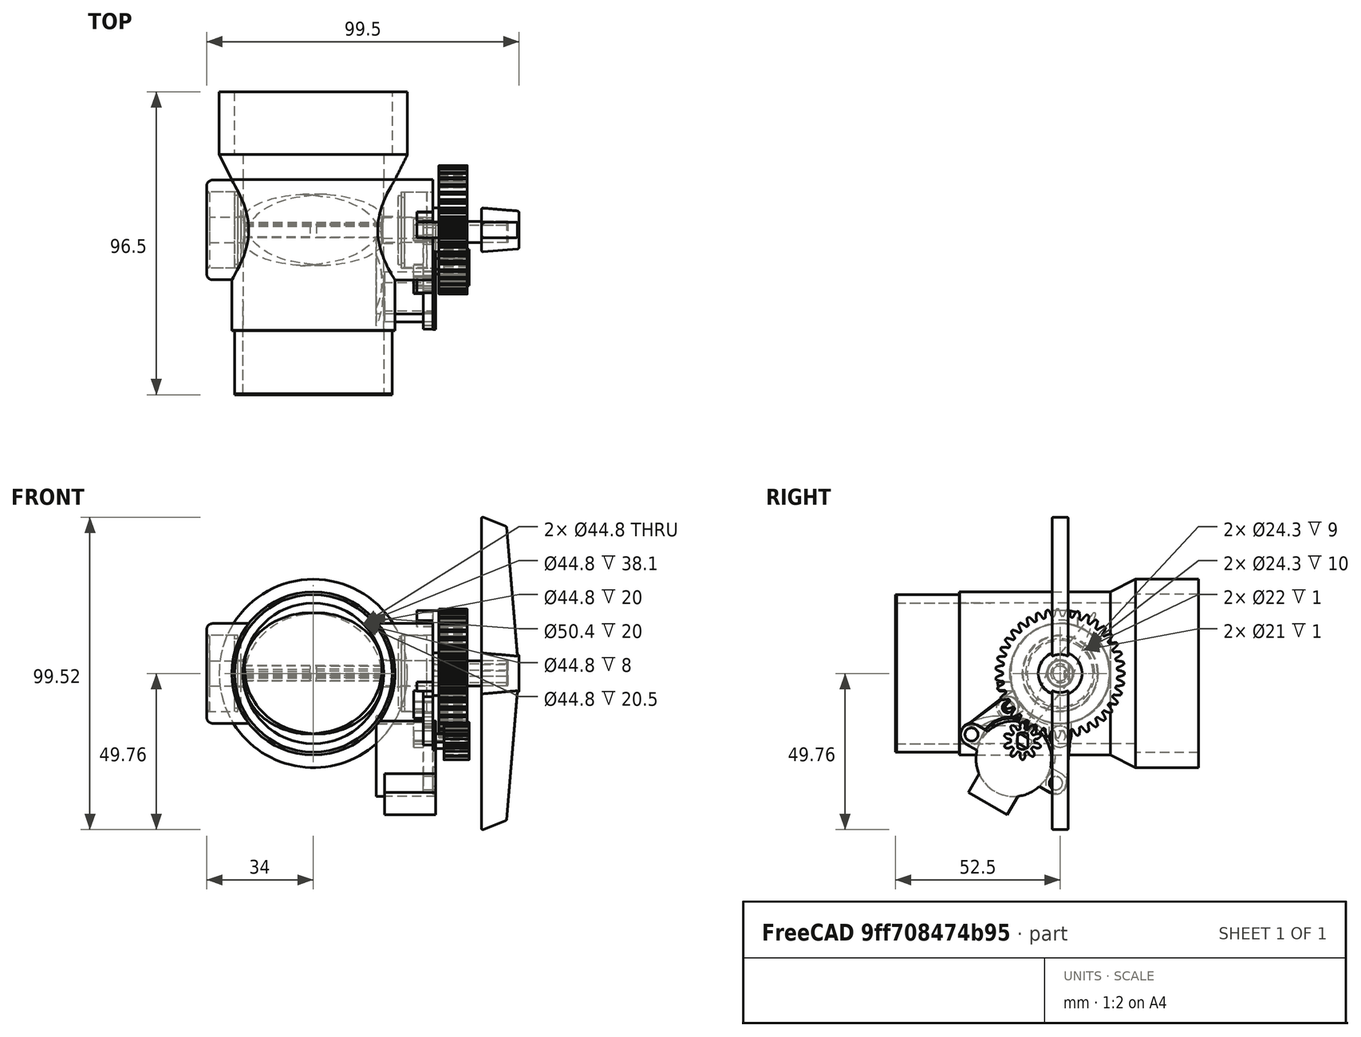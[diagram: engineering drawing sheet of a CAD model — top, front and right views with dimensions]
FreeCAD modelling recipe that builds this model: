
FCSTD DOCUMENT  (FreeCAD 0.20R29603 (Git))
Label: Pellet Sorter butterfly valve
License: All rights reserved
LicenseURL: http://en.wikipedia.org/wiki/All_rights_reserved
objects: Sketcher::SketchObject×59, PartDesign::Pad×34, PartDesign::Pocket×22, PartDesign::Body×17, PartDesign::Fillet×5, Part::Part2DObjectPython×4, PartDesign::Revolution×2, PartDesign::AdditiveLoft×2, PartDesign::Groove×1, PartDesign::Chamfer×1
note: 214 computed .brp shape members not serialized (recipe doc carries the construction recipe); baked Part::Feature solids carry a one-line shape summary decoded from their .brp

FEATURE [Sketcher::SketchObject] Sketch
  FullyConstrained = true
  MapMode = 5
  Placement = pos=(0,0,0) rot=(0.57735,0.57735,0.57735;2.0944rad)
  Support = -> [YZ_Plane]
  sketch-geometry (19):
    g0: ArcOfCircle CenterX=0 CenterY=0 CenterZ=0 NormalX=0 NormalY=0 NormalZ=1 AngleXU=0 Radius=4 StartAngle=2.97959 EndAngle=3.30359
    g1: ArcOfCircle CenterX=0 CenterY=0 CenterZ=0 NormalX=0 NormalY=0 NormalZ=1 AngleXU=0 Radius=2.5 StartAngle=0.573513 EndAngle=5.70967
    g2: LineSegment StartX=2.5 StartY=-6e-16 StartZ=0 EndX=4 EndY=-6e-16 EndZ=0
    g3: LineSegment StartX=-3.94763 StartY=0.645161 StartZ=0 EndX=-0.493454 EndY=21.7806 EndZ=0
    g4: LineSegment StartX=0.493454 StartY=21.7806 StartZ=0 EndX=3.94763 EndY=0.645161 EndZ=0
    g5: LineSegment StartX=-3.94763 StartY=-0.645161 StartZ=0 EndX=-0.493454 EndY=-21.7806 EndZ=0
    g6: LineSegment StartX=3.94763 StartY=-0.645161 StartZ=0 EndX=0.493454 EndY=-21.7806 EndZ=0
    g7: ArcOfCircle CenterX=0 CenterY=0 CenterZ=0 NormalX=0 NormalY=0 NormalZ=1 AngleXU=0 Radius=4 StartAngle=6.12119 EndAngle=6.44518
    g8: LineSegment StartX=2.1 StartY=1.35647 StartZ=0 EndX=2.1 EndY=0.45 EndZ=0
    g9: LineSegment StartX=2.1 StartY=0.45 StartZ=0 EndX=1.6 EndY=0.45 EndZ=0
    g10: LineSegment StartX=1.6 StartY=0.45 StartZ=0 EndX=1.6 EndY=-0.45 EndZ=0
    g11: LineSegment StartX=1.6 StartY=-0.45 StartZ=0 EndX=2.1 EndY=-0.45 EndZ=0
    g12: ArcOfCircle CenterX=0 CenterY=0 CenterZ=0 NormalX=0 NormalY=0 NormalZ=1 AngleXU=0 Radius=2.5 StartAngle=0 EndAngle=0.573513
    g13: ArcOfCircle CenterX=0 CenterY=0 CenterZ=0 NormalX=0 NormalY=0 NormalZ=1 AngleXU=0 Radius=2.5 StartAngle=5.70967 EndAngle=6.28319
    g14: LineSegment StartX=2.1 StartY=-0.45 StartZ=0 EndX=2.1 EndY=-1.35647 EndZ=0
    g15: ArcOfCircle CenterX=0 CenterY=21.7 CenterZ=0 NormalX=0 NormalY=0 NormalZ=1 AngleXU=0 Radius=0.5 StartAngle=0.161998 EndAngle=2.97959
    g16: ArcOfCircle CenterX=0 CenterY=-21.7 CenterZ=0 NormalX=0 NormalY=0 NormalZ=1 AngleXU=0 Radius=0.5 StartAngle=3.30359 EndAngle=6.12119
    g17: LineSegment StartX=0 StartY=21.7 StartZ=0 EndX=0 EndY=22.2 EndZ=0
    g18: LineSegment StartX=0 StartY=-21.7 StartZ=0 EndX=0 EndY=-22.2 EndZ=0
  constraints (51):
    c: Coincident(g0,g-1)
    c: Coincident(g1,g0)
    c: PointOnObject(g2,g0)
    c: Horizontal(g2)
    c: PointOnObject(g2,g-1)
    c: Distance(g2) = 1.5
    c: Diameter(g1) = 5
    c: Equal(g3,g5)
    c: Tangent(g0,g3) = 1.5708
    c: Equal(g0,g7)
    c: Tangent(g0,g5) = -1.5708
    c: Tangent(g7,g6) = 1.5708
    c: Coincident(g0,g7)
    c: Tangent(g7,g4) = 1.5708
    c: Vertical(g8)
    c: Horizontal(g9)
    c: Coincident(g10,g9)
    c: Vertical(g10)
    c: Coincident(g11,g10)
    c: Horizontal(g11)
    c: Coincident(g8,g9)
    c: Coincident(g1,g8)
    c: Coincident(g12,g0)
    c: Coincident(g12,g1)
    c: Coincident(g12,g2)
    c: Coincident(g13,g0)
    c: Coincident(g13,g1)
    c: Coincident(g13,g2)
    c: Equal(g11,g9)
    c: Coincident(g14,g11)
    c: Coincident(g14,g1)
    c: Vertical(g14)
    c: Equal(g8,g14)
    c: Distance(g0,g10) = 1.6
    c: Distance(g8,g-2) = 2.1
    c: Distance(g10) = 0.9
    c: PointOnObject(g15,g-2)
    c: PointOnObject(g16,g-2)
    c: Tangent(g15,g3) = 1.5708
    c: Tangent(g15,g4) = 1.5708
    c: Tangent(g16,g6) = 1.5708
    c: Tangent(g16,g5) = -1.5708
    c: Coincident(g17,g15)
    c: PointOnObject(g17,g15)
    c: Coincident(g18,g16)
    c: PointOnObject(g18,g16)
    c: Vertical(g18)
    c: Vertical(g17)
    c: Distance(g17,g18) = 44.4
    c: Equal(g15,g16)
    c: Diameter(g15) = 1
FEATURE [PartDesign::Pad] Pad
  Direction = (1,-2e-16,3e-16)
  Length = 44
  Length2 = 10
  Midplane = true
  Placement = pos=(0,0,0) rot=(0.57735,0.57735,0.57735;2.0944rad)
  Profile = -> Sketch
  ReferenceAxis = -> Sketch [N_Axis]
  Type = 0
FEATURE [Sketcher::SketchObject] Sketch001
  FullyConstrained = true
  MapMode = 5
  Placement = pos=(0,0,0) rot=(1,0,0;1.5708rad)
  Support = -> [XZ_Plane]
  sketch-geometry (8):
    g0: ArcOfCircle CenterX=0 CenterY=0 CenterZ=0 NormalX=0 NormalY=0 NormalZ=1 AngleXU=0 Radius=22.2 StartAngle=0.18117 EndAngle=2.96042
    g1: ArcOfCircle CenterX=0 CenterY=0 CenterZ=0 NormalX=0 NormalY=0 NormalZ=1 AngleXU=0 Radius=50 StartAngle=0 EndAngle=3.14159
    g2: LineSegment StartX=-50 StartY=6.1e-15 StartZ=0 EndX=-31.8367 EndY=0 EndZ=0
    g3: LineSegment StartX=-31.8367 StartY=0 StartZ=0 EndX=-31.8367 EndY=4 EndZ=0
    g4: LineSegment StartX=-31.8367 StartY=4 StartZ=0 EndX=-21.8367 EndY=4 EndZ=0
    g5: LineSegment StartX=21.8367 StartY=4 StartZ=0 EndX=31.8367 EndY=4 EndZ=0
    g6: LineSegment StartX=31.8367 StartY=4 StartZ=0 EndX=31.8367 EndY=0 EndZ=0
    g7: LineSegment StartX=31.8367 StartY=0 StartZ=0 EndX=50 EndY=0 EndZ=0
  constraints (24):
    c: Coincident(g0,g-1)
    c: Coincident(g1,g0)
    c: PointOnObject(g1,g-1)
    c: PointOnObject(g1,g-1)
    c: Coincident(g2,g1)
    c: PointOnObject(g2,g-1)
    c: Coincident(g3,g2)
    c: Vertical(g3)
    c: Coincident(g4,g3)
    c: Coincident(g4,g0)
    c: Horizontal(g4)
    c: Coincident(g5,g0)
    c: Horizontal(g5)
    c: Coincident(g6,g5)
    c: PointOnObject(g6,g-1)
    c: Vertical(g6)
    c: Coincident(g7,g6)
    c: Coincident(g7,g1)
    c: Diameter(g0) = 44.4
    c: Equal(g5,g4)
    c: Equal(g3,g6)
    c: Distance(g6) = 4
    c: Distance(g5) = 10
    c: Diameter(g1) = 100
FEATURE [PartDesign::Groove] Groove
  Angle = 360
  Axis = (1,0,0)
  Base = (0,0,0)
  BaseFeature = -> Pad
  Placement = pos=(0,0,0) rot=(0.57735,0.57735,0.57735;2.0944rad)
  Profile = -> Sketch001
  ReferenceAxis = -> X_Axis
  Reversed = true
FEATURE [Sketcher::SketchObject] Sketch002
  FullyConstrained = true
  MapMode = 5
  Placement = pos=(0,0,0) rot=(1,0,0;1.5708rad)
  Support = -> [XZ_Plane001]
  sketch-geometry (1):
    g0: Circle CenterX=0 CenterY=0 CenterZ=0 NormalX=0 NormalY=0 NormalZ=1 AngleXU=0 Radius=26
  constraints (2):
    c: Coincident(g0,g-1)
    c: Diameter(g0) = 52
FEATURE [PartDesign::Pad] Pad001
  Direction = (0,-1,2e-16)
  Length = 22.1
  Length2 = 16
  Placement = pos=(0,0,0) rot=(1,0,0;1.5708rad)
  Profile = -> Sketch002
  ReferenceAxis = -> Sketch002 [N_Axis]
  Type = 4
FEATURE [Sketcher::SketchObject] Sketch004
  FullyConstrained = true
  MapMode = 5
  Placement = pos=(0,0,0) rot=(1,0,0;1.5708rad)
  Support = -> [XZ_Plane001]
  sketch-geometry (4):
    g0: ArcOfCircle CenterX=0 CenterY=0 CenterZ=0 NormalX=0 NormalY=0 NormalZ=1 AngleXU=0 Radius=26 StartAngle=5.62031 EndAngle=6.28319
    g1: LineSegment StartX=20.4939 StartY=-16 StartZ=0 EndX=38 EndY=-16 EndZ=0
    g2: LineSegment StartX=38 StartY=-16 StartZ=0 EndX=38 EndY=0 EndZ=0
    g3: LineSegment StartX=38 StartY=0 StartZ=0 EndX=26 EndY=-6.4e-15 EndZ=0
  constraints (12):
    c: Coincident(g0,g-1)
    c: PointOnObject(g0,g-1)
    c: Coincident(g1,g0)
    c: Horizontal(g1)
    c: Coincident(g2,g1)
    c: PointOnObject(g2,g-1)
    c: Vertical(g2)
    c: Coincident(g3,g2)
    c: Coincident(g3,g0)
    c: Diameter(g0) = 52
    c: Distance(g3) = 12
    c: Distance(g2) = 16
FEATURE [PartDesign::Revolution] Revolution
  Angle = 360
  Axis = (1,0,0)
  Base = (0,0,0)
  BaseFeature = -> Pad001
  Placement = pos=(0,0,0) rot=(1,0,0;1.5708rad)
  Profile = -> Sketch004
  ReferenceAxis = -> Sketch004 [H_Axis]
  Reversed = true
FEATURE [Sketcher::SketchObject] Sketch006
  FullyConstrained = true
  MapMode = 5
  Placement = pos=(38,0,0) rot=(0.707107,0,0.707107;3.14159rad)
  sketch-geometry (1):
    g0: Circle CenterX=0 CenterY=0 CenterZ=0 NormalX=0 NormalY=0 NormalZ=1 AngleXU=0 Radius=12.15
  constraints (2):
    c: Coincident(g0,g-1)
    c: Diameter(g0) = 24.3
FEATURE [PartDesign::Pocket] Pocket001
  BaseFeature = -> Revolution
  Direction = (-1,0,2e-16)
  Length = 10
  Length2 = 5
  Placement = pos=(0,0,0) rot=(1,0,0;1.5708rad)
  Profile = -> Sketch006
  ReferenceAxis = -> Sketch006 [N_Axis]
  Type = 0
FEATURE [Sketcher::SketchObject] Sketch007
  FullyConstrained = true
  MapMode = 5
  Placement = pos=(28,0,0) rot=(0.707107,0,0.707107;3.14159rad)
  Support = -> [Pocket001]
  sketch-geometry (1):
    g0: Circle CenterX=0 CenterY=0 CenterZ=0 NormalX=0 NormalY=0 NormalZ=1 AngleXU=0 Radius=11
  constraints (2):
    c: Coincident(g0,g-1)
    c: Diameter(g0) = 22
FEATURE [PartDesign::Pocket] Pocket002
  BaseFeature = -> Pocket001
  Direction = (-1,0,2e-16)
  Length = 1
  Length2 = 5
  Placement = pos=(0,0,0) rot=(1,0,0;1.5708rad)
  Profile = -> Sketch007
  ReferenceAxis = -> Sketch007 [N_Axis]
  Type = 0
FEATURE [Sketcher::SketchObject] Sketch008
  FullyConstrained = true
  MapMode = 5
  Placement = pos=(27,0,-5.9e-15) rot=(0.707107,0,0.707107;3.14159rad)
  Support = -> [Pocket002]
  sketch-geometry (1):
    g0: Circle CenterX=0 CenterY=0 CenterZ=0 NormalX=0 NormalY=0 NormalZ=1 AngleXU=0 Radius=4.2
  constraints (2):
    c: Coincident(g0,g-1)
    c: Diameter(g0) = 8.4
FEATURE [PartDesign::Pocket] Pocket003
  BaseFeature = -> Pocket002
  Direction = (-1,0,2e-16)
  Length = 10
  Length2 = 5
  Placement = pos=(0,0,0) rot=(1,0,0;1.5708rad)
  Profile = -> Sketch008
  ReferenceAxis = -> Sketch008 [N_Axis]
  Type = 0
FEATURE [Sketcher::SketchObject] Sketch009
  FullyConstrained = true
  MapMode = 5
  Placement = pos=(0,0,0) rot=(0.57735,0.57735,0.57735;2.0944rad)
  Support = -> [YZ_Plane002]
  sketch-geometry (1):
    g0: Circle CenterX=0 CenterY=0 CenterZ=0 NormalX=0 NormalY=0 NormalZ=1 AngleXU=0 Radius=4
  constraints (2):
    c: Coincident(g0,g-1)
    c: Diameter(g0) = 8
FEATURE [PartDesign::Pad] Pad002
  Direction = (1,-2e-16,3e-16)
  Length = 40
  Length2 = 10
  Placement = pos=(0,0,0) rot=(0.57735,0.57735,0.57735;2.0944rad)
  Profile = -> Sketch009
  ReferenceAxis = -> Sketch009 [N_Axis]
  Type = 0
FEATURE [Sketcher::SketchObject] Sketch010
  FullyConstrained = true
  MapMode = 5
  Support = -> [XY_Plane003]
  sketch-geometry (2):
    g0: Circle CenterX=0 CenterY=0 CenterZ=0 NormalX=0 NormalY=0 NormalZ=1 AngleXU=0 Radius=4
    g1: Circle CenterX=0 CenterY=0 CenterZ=0 NormalX=0 NormalY=0 NormalZ=1 AngleXU=0 Radius=12
  constraints (4):
    c: Coincident(g0,g-1)
    c: Coincident(g1,g0)
    c: Diameter(g0) = 8
    c: Diameter(g1) = 24
FEATURE [PartDesign::Pad] Pad003
  Direction = (0,0,1)
  Length = 8.1
  Length2 = 10
  Profile = -> Sketch010
  ReferenceAxis = -> Sketch010 [N_Axis]
  Type = 0
FEATURE [PartDesign::Body] Body003  label="Body002: Bearing"
  Group = -> [Sketch010,Pad003]
  Origin = -> Origin003
  Placement = pos=(28,0,-1.4e-14) rot=(0,1,0;1.5708rad)
  Tip = -> Pad003
FEATURE [Sketcher::SketchObject] Sketch011
  FullyConstrained = true
  MapMode = 5
  Placement = pos=(0,0,0) rot=(0.57735,0.57735,0.57735;2.0944rad)
  Support = -> [YZ_Plane002]
  sketch-geometry (6):
    g0: ArcOfCircle CenterX=0 CenterY=0 CenterZ=0 NormalX=0 NormalY=0 NormalZ=1 AngleXU=0 Radius=2.3 StartAngle=0.598668 EndAngle=5.68452
    g1: LineSegment StartX=1.9 StartY=1.29615 StartZ=0 EndX=1.9 EndY=0.65 EndZ=0
    g2: LineSegment StartX=1.9 StartY=0.65 StartZ=0 EndX=1.4 EndY=0.65 EndZ=0
    g3: LineSegment StartX=1.4 StartY=0.65 StartZ=0 EndX=1.4 EndY=-0.65 EndZ=0
    g4: LineSegment StartX=1.9 StartY=-0.65 StartZ=0 EndX=1.9 EndY=-1.29615 EndZ=0
    g5: LineSegment StartX=1.4 StartY=-0.65 StartZ=0 EndX=1.9 EndY=-0.65 EndZ=0
  constraints (18):
    c: Coincident(g0,g-1)
    c: Diameter(g0) = 4.6
    c: Vertical(g1)
    c: Coincident(g2,g1)
    c: Horizontal(g2)
    c: Coincident(g3,g2)
    c: Vertical(g3)
    c: Vertical(g4)
    c: Equal(g1,g4)
    c: Coincident(g0,g4)
    c: Coincident(g0,g1)
    c: Distance(g0,g3) = 1.4
    c: Distance(g1,g-2) = 1.9
    c: Coincident(g5,g3)
    c: Coincident(g5,g4)
    c: Horizontal(g5)
    c: Equal(g2,g5)
    c: Distance(g1,g4) = 1.3
FEATURE [PartDesign::Pad] Pad004
  BaseFeature = -> Pad002
  Direction = (1,-2e-16,3e-16)
  Length = 21
  Length2 = 10
  Placement = pos=(0,0,0) rot=(0.57735,0.57735,0.57735;2.0944rad)
  Profile = -> Sketch011
  ReferenceAxis = -> Sketch011 [N_Axis]
  Reversed = true
  Type = 0
FEATURE [Sketcher::SketchObject] Sketch012
  FullyConstrained = true
  MapMode = 5
  Placement = pos=(0,0,0) rot=(1,0,0;1.5708rad)
  Support = -> [XZ_Plane001]
  sketch-geometry (4):
    g0: ArcOfCircle CenterX=0 CenterY=0 CenterZ=0 NormalX=0 NormalY=0 NormalZ=1 AngleXU=0 Radius=26 StartAngle=2.48844 EndAngle=3.14159
    g1: LineSegment StartX=-26 StartY=0 StartZ=0 EndX=-34 EndY=0 EndZ=0
    g2: LineSegment StartX=-34 StartY=0 StartZ=0 EndX=-34 EndY=15.8 EndZ=0
    g3: LineSegment StartX=-34 StartY=15.8 StartZ=0 EndX=-20.6485 EndY=15.8 EndZ=0
  constraints (12):
    c: Coincident(g0,g-1)
    c: PointOnObject(g0,g-1)
    c: Coincident(g1,g0)
    c: Horizontal(g1)
    c: Coincident(g2,g1)
    c: Vertical(g2)
    c: Coincident(g3,g2)
    c: Coincident(g3,g0)
    c: Horizontal(g3)
    c: Diameter(g0) = 52
    c: Distance(g2) = 15.8
    c: Distance(g1) = 8
FEATURE [PartDesign::Revolution] Revolution001
  Angle = 360
  Axis = (1,0,0)
  Base = (0,0,0)
  BaseFeature = -> Pocket003
  Placement = pos=(0,0,0) rot=(1,0,0;1.5708rad)
  Profile = -> Sketch012
  ReferenceAxis = -> Sketch012 [H_Axis]
FEATURE [Sketcher::SketchObject] Sketch013
  FullyConstrained = true
  MapMode = 5
  Placement = pos=(0,0,0) rot=(1,0,0;1.5708rad)
  Support = -> [XZ_Plane001]
  sketch-geometry (1):
    g0: Circle CenterX=0 CenterY=0 CenterZ=0 NormalX=0 NormalY=0 NormalZ=1 AngleXU=0 Radius=22.4
  constraints (2):
    c: Coincident(g0,g-1)
    c: Diameter(g0) = 44.8
FEATURE [PartDesign::Pocket] Pocket
  BaseFeature = -> Revolution001
  Direction = (0,1,-2e-16)
  Length = 5
  Length2 = 5
  Midplane = true
  Placement = pos=(0,0,0) rot=(1,0,0;1.5708rad)
  Profile = -> Sketch013
  ReferenceAxis = -> Sketch013 [N_Axis]
  Type = 1
FEATURE [Sketcher::SketchObject] Sketch014
  FullyConstrained = true
  MapMode = 5
  Placement = pos=(-34,0,0) rot=(0.707107,0,-0.707107;3.14159rad)
  Support = -> [Pocket]
  sketch-geometry (1):
    g0: Circle CenterX=0 CenterY=0 CenterZ=0 NormalX=0 NormalY=0 NormalZ=1 AngleXU=0 Radius=12.15
  constraints (2):
    c: Coincident(g0,g-1)
    c: Diameter(g0) = 24.3
FEATURE [PartDesign::Pocket] Pocket004
  BaseFeature = -> Pocket
  Direction = (1,0,2e-16)
  Length = 9
  Length2 = 5
  Placement = pos=(0,0,0) rot=(1,0,0;1.5708rad)
  Profile = -> Sketch014
  ReferenceAxis = -> Sketch014 [N_Axis]
  Type = 0
FEATURE [Sketcher::SketchObject] Sketch015
  FullyConstrained = true
  MapMode = 5
  Placement = pos=(-25,0,0) rot=(0.707107,0,-0.707107;3.14159rad)
  Support = -> [Pocket004]
  sketch-geometry (1):
    g0: Circle CenterX=0 CenterY=0 CenterZ=0 NormalX=0 NormalY=0 NormalZ=1 AngleXU=0 Radius=11
  constraints (2):
    c: Coincident(g0,g-1)
    c: Diameter(g0) = 22
FEATURE [PartDesign::Pocket] Pocket005
  BaseFeature = -> Pocket004
  Direction = (1,0,2e-16)
  Length = 1
  Length2 = 5
  Placement = pos=(0,0,0) rot=(1,0,0;1.5708rad)
  Profile = -> Sketch015
  ReferenceAxis = -> Sketch015 [N_Axis]
  Type = 0
FEATURE [Sketcher::SketchObject] Sketch016
  FullyConstrained = true
  MapMode = 5
  Placement = pos=(-24,0,-5.3e-15) rot=(0.707107,0,-0.707107;3.14159rad)
  Support = -> [Pocket005]
  sketch-geometry (1):
    g0: Circle CenterX=0 CenterY=0 CenterZ=0 NormalX=0 NormalY=0 NormalZ=1 AngleXU=0 Radius=4.2
  constraints (2):
    c: Coincident(g0,g-1)
    c: Diameter(g0) = 8.4
FEATURE [PartDesign::Pocket] Pocket006
  BaseFeature = -> Pocket005
  Direction = (1,0,2e-16)
  Length = 10
  Length2 = 5
  Placement = pos=(0,0,0) rot=(1,0,0;1.5708rad)
  Profile = -> Sketch016
  ReferenceAxis = -> Sketch016 [N_Axis]
  Type = 0
FEATURE [Sketcher::SketchObject] Sketch017
  FullyConstrained = true
  MapMode = 5
  Placement = pos=(0,0,0) rot=(0.57735,0.57735,0.57735;2.0944rad)
  Support = -> [YZ_Plane004]
  sketch-geometry (1):
    g0: Circle CenterX=0 CenterY=0 CenterZ=0 NormalX=0 NormalY=0 NormalZ=1 AngleXU=0 Radius=4
  constraints (2):
    c: Coincident(g0,g-1)
    c: Diameter(g0) = 8
FEATURE [PartDesign::Pad] Pad005
  Direction = (1,-2e-16,3e-16)
  Length = 12
  Length2 = 10
  Placement = pos=(0,0,0) rot=(0.57735,0.57735,0.57735;2.0944rad)
  Profile = -> Sketch017
  ReferenceAxis = -> Sketch017 [N_Axis]
  Type = 0
FEATURE [Sketcher::SketchObject] Sketch018
  FullyConstrained = true
  MapMode = 5
  Placement = pos=(0,0,0) rot=(0.57735,0.57735,0.57735;2.0944rad)
  Support = -> [YZ_Plane004]
  sketch-geometry (6):
    g0: ArcOfCircle CenterX=0 CenterY=0 CenterZ=0 NormalX=0 NormalY=0 NormalZ=1 AngleXU=0 Radius=2.3 StartAngle=0.598668 EndAngle=5.68452
    g1: LineSegment StartX=1.9 StartY=1.29615 StartZ=0 EndX=1.9 EndY=0.65 EndZ=0
    g2: LineSegment StartX=1.9 StartY=0.65 StartZ=0 EndX=1.4 EndY=0.65 EndZ=0
    g3: LineSegment StartX=1.4 StartY=0.65 StartZ=0 EndX=1.4 EndY=-0.65 EndZ=0
    g4: LineSegment StartX=1.9 StartY=-0.65 StartZ=0 EndX=1.9 EndY=-1.29615 EndZ=0
    g5: LineSegment StartX=1.4 StartY=-0.65 StartZ=0 EndX=1.9 EndY=-0.65 EndZ=0
  constraints (18):
    c: Coincident(g0,g-1)
    c: Diameter(g0) = 4.6
    c: Vertical(g1)
    c: Coincident(g2,g1)
    c: Horizontal(g2)
    c: Coincident(g3,g2)
    c: Vertical(g3)
    c: Vertical(g4)
    c: Equal(g1,g4)
    c: Coincident(g0,g4)
    c: Coincident(g0,g1)
    c: Distance(g0,g3) = 1.4
    c: Distance(g1,g-2) = 1.9
    c: Coincident(g5,g3)
    c: Coincident(g5,g4)
    c: Horizontal(g5)
    c: Equal(g2,g5)
    c: Distance(g1,g4) = 1.3
FEATURE [PartDesign::Pad] Pad006
  BaseFeature = -> Pad005
  Direction = (1,-2e-16,3e-16)
  Length = 21
  Length2 = 10
  Placement = pos=(0,0,0) rot=(0.57735,0.57735,0.57735;2.0944rad)
  Profile = -> Sketch018
  ReferenceAxis = -> Sketch018 [N_Axis]
  Reversed = true
  Type = 0
FEATURE [Sketcher::SketchObject] Sketch020
  FullyConstrained = true
  MapMode = 5
  Placement = pos=(12,-2.6e-15,2.6e-15) rot=(0.57735,0.57735,0.57735;2.0944rad)
  Support = -> [Pad006]
  sketch-geometry (1):
    g0: Circle CenterX=0 CenterY=0 CenterZ=0 NormalX=0 NormalY=0 NormalZ=1 AngleXU=0 Radius=11.9
  constraints (2):
    c: Coincident(g0,g-1)
    c: Diameter(g0) = 23.8
FEATURE [PartDesign::Pad] Pad007
  BaseFeature = -> Pad006
  Direction = (1,-9e-16,6e-16)
  Length = 1
  Length2 = 10
  Placement = pos=(0,0,0) rot=(0.57735,0.57735,0.57735;2.0944rad)
  Profile = -> Sketch020
  ReferenceAxis = -> Sketch020 [N_Axis]
  Reversed = true
  Type = 0
FEATURE [PartDesign::Body] Body004  label="Body002: Pin v0"
  Group = -> [Sketch017,Pad005,Sketch018,Pad006,Sketch020,Pad007]
  Origin = -> Origin004
  Placement = pos=(-22,0,-1.2e-14) rot=(0,1,0;3.14159rad)
  Tip = -> Pad007
FEATURE [Sketcher::SketchObject] Sketch021
  FullyConstrained = true
  MapMode = 5
  Placement = pos=(40,-8.8e-15,8.8e-15) rot=(0.57735,0.57735,0.57735;2.0944rad)
  Support = -> [Pad004]
  sketch-geometry (7):
    g0: Circle CenterX=0 CenterY=0 CenterZ=0 NormalX=0 NormalY=0 NormalZ=1 AngleXU=0 Radius=4
    g1: LineSegment StartX=1.4 StartY=-1 StartZ=0 EndX=1.4 EndY=1 EndZ=0
    g2: LineSegment StartX=1.4 StartY=1 StartZ=0 EndX=2.7 EndY=1 EndZ=0
    g3: LineSegment StartX=2.7 StartY=1 StartZ=0 EndX=2.7 EndY=2.95127 EndZ=0
    g4: LineSegment StartX=1.4 StartY=-1 StartZ=0 EndX=2.7 EndY=-1 EndZ=0
    g5: LineSegment StartX=2.7 StartY=-1 StartZ=0 EndX=2.7 EndY=-2.95127 EndZ=0
    g6: ArcOfCircle CenterX=0 CenterY=0 CenterZ=0 NormalX=0 NormalY=0 NormalZ=1 AngleXU=0 Radius=4 StartAngle=5.45335 EndAngle=7.11302
  constraints (20):
    c: Coincident(g0,g-1)
    c: Vertical(g1)
    c: Coincident(g2,g1)
    c: Horizontal(g2)
    c: Coincident(g3,g2)
    c: PointOnObject(g3,g0)
    c: Vertical(g3)
    c: Coincident(g4,g1)
    c: Horizontal(g4)
    c: Coincident(g5,g4)
    c: Vertical(g5)
    c: Equal(g3,g5)
    c: Equal(g4,g2)
    c: Distance(g0,g1) = 1.4
    c: Distance(g2,g4) = 2
    c: Distance(g4,g-2) = 2.7
    c: Diameter(g0) = 8
    c: Coincident(g6,g0)
    c: Coincident(g6,g3)
    c: Coincident(g6,g5)
FEATURE [PartDesign::Pocket] Pocket007
  BaseFeature = -> Pad004
  Direction = (-1,9e-16,-6e-16)
  Length = 24
  Length2 = 5
  Placement = pos=(0,0,0) rot=(0.57735,0.57735,0.57735;2.0944rad)
  Profile = -> Sketch021
  ReferenceAxis = -> Sketch021 [N_Axis]
  Type = 0
FEATURE [PartDesign::Body] Body002  label="Body002: Shaft v0"
  Group = -> [Sketch009,Pad002,Sketch011,Pad004,Sketch021,Pocket007]
  Origin = -> Origin002
  Placement = pos=(22,0,0) rot=(0,0,1;0rad)
  Tip = -> Pocket007
FEATURE [PartDesign::Chamfer] Chamfer
  Angle = 45
  Base = -> Groove [Edge27,Edge26,Edge29,Edge11,Edge28,Edge46,Edge44,Edge21,Edge47,Edge45]
  BaseFeature = -> Groove
  ChamferType = 1
  FlipDirection = true
  Placement = pos=(0,0,0) rot=(0.57735,0.57735,0.57735;2.0944rad)
  Size = 0.16
  Size2 = 1
  SupportTransform = false
  UseAllEdges = false
FEATURE [PartDesign::Body] Body  label="Body: Butterfly v0"
  Group = -> [Sketch,Pad,Sketch001,Groove,Chamfer]
  Origin = -> Origin
  Placement = pos=(0,0,0) rot=(-1,0,0;0.523599rad)
  Tip = -> Chamfer
FEATURE [Sketcher::SketchObject] Sketch060
  AttachmentOffset = pos=(0,0,0) rot=(0,0,-1;3.14159rad)
  FullyConstrained = true
  MapMode = 5
  Placement = pos=(38,0,0) rot=(0,1,0;1.5708rad)
  Support = -> [Pocket006]
  sketch-geometry (8):
    g0: ArcOfCircle CenterX=0 CenterY=0 CenterZ=0 NormalX=0 NormalY=0 NormalZ=1 AngleXU=0 Radius=16 StartAngle=4.88195 EndAngle=5.07664
    g1: LineSegment StartX=2.7 StartY=-15.7705 StartZ=0 EndX=2.7 EndY=-19.9683 EndZ=0
    g2: LineSegment StartX=5.7 StartY=-14.9503 StartZ=0 EndX=5.7 EndY=-19.327 EndZ=0
    g3: ArcOfCircle CenterX=0 CenterY=0 CenterZ=0 NormalX=0 NormalY=0 NormalZ=1 AngleXU=0 Radius=20.15 StartAngle=4.84679 EndAngle=4.99918
    g4: ArcOfCircle CenterX=0 CenterY=0 CenterZ=0 NormalX=0 NormalY=0 NormalZ=1 AngleXU=0 Radius=16 StartAngle=2.77734 EndAngle=2.97203
    g5: ArcOfCircle CenterX=0 CenterY=0 CenterZ=0 NormalX=0 NormalY=0 NormalZ=1 AngleXU=0 Radius=20.15 StartAngle=2.8548 EndAngle=3.00719
    g6: LineSegment StartX=-19.9683 StartY=2.7 StartZ=0 EndX=-15.7705 EndY=2.7 EndZ=0
    g7: LineSegment StartX=-14.9503 StartY=5.7 StartZ=0 EndX=-19.327 EndY=5.7 EndZ=0
  constraints (24):
    c: Coincident(g0,g-1)
    c: Diameter(g0) = 32
    c: Coincident(g1,g0)
    c: Vertical(g1)
    c: Coincident(g2,g0)
    c: Vertical(g2)
    c: Coincident(g3,g0)
    c: Coincident(g3,g1)
    c: Coincident(g3,g2)
    c: Diameter(g3) = 40.3
    c: Distance(g0,g-2) = 2.7
    c: Distance(g2,g1) = 3
    c: Coincident(g4,g0)
    c: Coincident(g5,g0)
    c: Coincident(g6,g5)
    c: Coincident(g6,g4)
    c: Horizontal(g6)
    c: Coincident(g7,g4)
    c: Horizontal(g7)
    c: Coincident(g5,g7)
    c: Equal(g4,g0)
    c: Equal(g5,g3)
    c: Equal(g7,g2)
    c: Equal(g6,g1)
FEATURE [PartDesign::Pad] Pad008
  BaseFeature = -> Pocket006
  Direction = (1,0,-2e-16)
  Length = 5
  Length2 = 10
  Placement = pos=(0,0,0) rot=(1,0,0;1.5708rad)
  Profile = -> Sketch060
  ReferenceAxis = -> Sketch060 [N_Axis]
  Reversed = true
  Type = 0
FEATURE [Sketcher::SketchObject] Sketch031
  FullyConstrained = true
  MapMode = 5
  Support = -> [XY_Plane006]
  sketch-geometry (14):
    g0: ArcOfCircle CenterX=0 CenterY=0 CenterZ=0 NormalX=0 NormalY=0 NormalZ=1 AngleXU=0 Radius=7 StartAngle=1.936 EndAngle=7.48877
    g1: LineSegment StartX=-2.5 StartY=6.53835 StartZ=0 EndX=-2.5 EndY=20 EndZ=0
    g2: LineSegment StartX=2.5 StartY=6.53835 StartZ=0 EndX=2.5 EndY=20 EndZ=0
    g3: LineSegment StartX=2.5 StartY=20 StartZ=0 EndX=-2.5 EndY=20 EndZ=0
    g4: LineSegment StartX=0 StartY=0 StartZ=0 EndX=0 EndY=20 EndZ=0
    g5: ArcOfCircle CenterX=0 CenterY=0 CenterZ=0 NormalX=0 NormalY=0 NormalZ=1 AngleXU=0 Radius=4 StartAngle=0.795399 EndAngle=5.48779
    g6: LineSegment StartX=2.8 StartY=-2.85657 StartZ=0 EndX=2.8 EndY=-0.85 EndZ=0
    g7: LineSegment StartX=2.8 StartY=-0.85 StartZ=0 EndX=1.5 EndY=-0.85 EndZ=0
    g8: LineSegment StartX=1.5 StartY=-0.85 StartZ=0 EndX=1.5 EndY=0.85 EndZ=0
    g9: LineSegment StartX=1.5 StartY=0.85 StartZ=0 EndX=2.8 EndY=0.85 EndZ=0
    g10: LineSegment StartX=2.8 StartY=0.85 StartZ=0 EndX=2.8 EndY=2.85657 EndZ=0
    g11: LineSegment StartX=-4 StartY=0 StartZ=0 EndX=1.5 EndY=0 EndZ=0
    g12: LineSegment StartX=2.8 StartY=-0.85 StartZ=0 EndX=2.8 EndY=0.85 EndZ=0
    g13: LineSegment StartX=2.8 StartY=0 StartZ=0 EndX=-4 EndY=0 EndZ=0
  constraints (43):
    c: Vertical(g1)
    c: Vertical(g2)
    c: Coincident(g3,g2)
    c: Coincident(g3,g1)
    c: Horizontal(g3)
    c: Coincident(g0,g2)
    c: Coincident(g0,g1)
    c: Diameter(g0) = 14
    c: Distance(g3) = 5
    c: Equal(g1,g2)
    c: Coincident(g4,g0)
    c: Vertical(g4)
    c: Distance(g4) = 20
    c: PointOnObject(g4,g3)
    c: Coincident(g0,g-1)
    c: Coincident(g5,g0)
    c: Diameter(g5) = 8
    c: Vertical(g6)
    c: Coincident(g7,g6)
    c: Horizontal(g7)
    c: Vertical(g8)
    c: Coincident(g9,g8)
    c: Horizontal(g9)
    c: Coincident(g10,g9)
    c: Vertical(g10)
    c: PointOnObject(g11,g5)
    c: PointOnObject(g11,g8)
    c: Horizontal(g11)
    c: Perpendicular(g5,g11)
    c: Distance(g11) = 5.5
    c: Coincident(g12,g6)
    c: Coincident(g12,g9)
    c: Vertical(g12)
    c: PointOnObject(g13,g12)
    c: PointOnObject(g13,g5)
    c: Horizontal(g13)
    c: Perpendicular(g5,g13)
    c: Distance(g13) = 6.8
    c: Distance(g12) = 1.7
    c: Equal(g10,g6)
    c: Coincident(g7,g8)
    c: Coincident(g5,g6)
    c: Coincident(g5,g10)
FEATURE [PartDesign::Pad] Pad011
  Direction = (0,0,1)
  Length = 2
  Length2 = 10
  Profile = -> Sketch031
  ReferenceAxis = -> Sketch031 [N_Axis]
  Type = 0
FEATURE [Sketcher::SketchObject] Sketch032
  FullyConstrained = true
  MapMode = 5
  Placement = pos=(0,0,0) rot=(1,0,0;3.14159rad)
  Support = -> [Pad011]
  sketch-geometry (5):
    g0: LineSegment StartX=0 StartY=-20 StartZ=0 EndX=2.5 EndY=-20 EndZ=0
    g1: LineSegment StartX=0 StartY=-20 StartZ=0 EndX=-2.5 EndY=-20 EndZ=0
    g2: LineSegment StartX=-2.5 StartY=-20 StartZ=0 EndX=-2.5 EndY=-16.8152 EndZ=0
    g3: LineSegment StartX=2.5 StartY=-20 StartZ=0 EndX=2.5 EndY=-16.8152 EndZ=0
    g4: ArcOfCircle CenterX=0 CenterY=0 CenterZ=0 NormalX=0 NormalY=0 NormalZ=1 AngleXU=0 Radius=17 StartAngle=4.56479 EndAngle=4.85998
  constraints (15):
    c: PointOnObject(g0,g-2)
    c: Horizontal(g0)
    c: Coincident(g1,g0)
    c: Horizontal(g1)
    c: Coincident(g2,g1)
    c: Vertical(g2)
    c: Coincident(g3,g0)
    c: Vertical(g3)
    c: Coincident(g4,g-1)
    c: Coincident(g4,g3)
    c: Coincident(g4,g2)
    c: Equal(g3,g2)
    c: Distance(g0,g1) = 5
    c: Diameter(g4) = 34
    c: Distance(g4,g0) = 20
FEATURE [PartDesign::Pad] Pad012
  BaseFeature = -> Pad011
  Direction = (0,0,-1)
  Length = 5
  Length2 = 10
  Profile = -> Sketch032
  ReferenceAxis = -> Sketch032 [N_Axis]
  Type = 0
FEATURE [PartDesign::Body] Body006  label="Body006: Ball stop"
  Group = -> [Sketch031,Pad011,Sketch032,Pad012]
  Origin = -> Origin006
  Placement = pos=(38,-2.8e-14,-2.6e-14) rot=(0.57735,0.57735,0.57735;2.0944rad)
  Tip = -> Pad012
FEATURE [PartDesign::Fillet] Fillet
  Base = -> Pad008 [Edge24]
  BaseFeature = -> Pad008
  Placement = pos=(0,0,0) rot=(1,0,0;1.5708rad)
  Radius = 2
  SupportTransform = false
  UseAllEdges = false
FEATURE [Sketcher::SketchObject] Sketch061
  FullyConstrained = false
  MapMode = 5
  Placement = pos=(38,0,0) rot=(0.707107,0,0.707107;3.14159rad)
  Support = -> [Fillet]
  sketch-geometry (4):
    g0: Circle CenterX=-27.2 CenterY=14.8 CenterZ=0 NormalX=0 NormalY=0 NormalZ=1 AngleXU=0 Radius=12
    g1: LineSegment StartX=-27.2 StartY=14.8 StartZ=0 EndX=0 EndY=0 EndZ=0
    g2: LineSegment StartX=-27.2 StartY=14.8 StartZ=0 EndX=-34.6521 EndY=1.89256 EndZ=0
    g3: LineSegment StartX=-27.2 StartY=14.8 StartZ=0 EndX=-19.5784 EndY=28.001 EndZ=0
  constraints (9):
    c: Diameter(g0) = 24
    c: Distance(g0,g-2) = 27.2
    c: Distance(g0,g-1) = 14.8
    c: Coincident(g1,g0)
    c: Coincident(g1,g-1)
    c: Coincident(g2,g0)
    c: Coincident(g3,g0)
    c: Parallel(g3,g2)
    c: Angle(g-1,g2) = 1.0472
FEATURE [Sketcher::SketchObject] Sketch034
  FullyConstrained = true
  MapMode = 5
  Support = -> [XY_Plane007]
  sketch-geometry (1):
    g0: Circle CenterX=0 CenterY=0 CenterZ=0 NormalX=0 NormalY=0 NormalZ=1 AngleXU=0 Radius=12
  constraints (2):
    c: Coincident(g0,g-1)
    c: Diameter(g0) = 24
FEATURE [PartDesign::Pad] Pad014
  Direction = (0,0,1)
  Length = 19
  Length2 = 10
  Profile = -> Sketch034
  ReferenceAxis = -> Sketch034 [N_Axis]
  Type = 0
FEATURE [Sketcher::SketchObject] Sketch035
  FullyConstrained = true
  MapMode = 5
  Placement = pos=(0,0,19) rot=(0,0,1;0rad)
  Support = -> [Pad014]
  sketch-geometry (5):
    g0: LineSegment StartX=-7.15 StartY=-6.5 StartZ=0 EndX=-7.15 EndY=-16.5 EndZ=0
    g1: LineSegment StartX=-7.15 StartY=-16.5 StartZ=0 EndX=7.15 EndY=-16.5 EndZ=0
    g2: LineSegment StartX=7.15 StartY=-16.5 StartZ=0 EndX=7.15 EndY=-6.5 EndZ=0
    g3: LineSegment StartX=7.15 StartY=-6.5 StartZ=0 EndX=-7.15 EndY=-6.5 EndZ=0
    g4: GeomPoint X=0 Y=-11.5 Z=0
  constraints (13):
    c: Coincident(g0,g1)
    c: Coincident(g1,g2)
    c: Coincident(g2,g3)
    c: Coincident(g3,g0)
    c: Horizontal(g1)
    c: Horizontal(g3)
    c: Vertical(g0)
    c: Vertical(g2)
    c: Symmetric(g1,g0,g4)
    c: PointOnObject(g4,g-2)
    c: DistanceY(g1,g-1) = 16.5
    c: DistanceX(g1,g1) = 14.3
    c: Distance(g2) = 10
FEATURE [PartDesign::Pad] Pad015
  BaseFeature = -> Pad014
  Direction = (0,0,1)
  Length = 16.3
  Length2 = 10
  Profile = -> Sketch035
  ReferenceAxis = -> Sketch035 [N_Axis]
  Reversed = true
  Type = 0
FEATURE [Sketcher::SketchObject] Sketch036
  FullyConstrained = true
  MapMode = 5
  Placement = pos=(0,0,19) rot=(0,0,1;0rad)
  Support = -> [Pad015]
  sketch-geometry (6):
    g0: Circle CenterX=15.5 CenterY=0 CenterZ=0 NormalX=0 NormalY=0 NormalZ=1 AngleXU=0 Radius=2.1
    g1: Circle CenterX=-15.5 CenterY=0 CenterZ=0 NormalX=0 NormalY=0 NormalZ=1 AngleXU=0 Radius=2.1
    g2: ArcOfCircle CenterX=15.5 CenterY=0 CenterZ=0 NormalX=0 NormalY=0 NormalZ=1 AngleXU=0 Radius=3.5 StartAngle=4.71239 EndAngle=7.85398
    g3: ArcOfCircle CenterX=-15.5 CenterY=0 CenterZ=0 NormalX=0 NormalY=0 NormalZ=1 AngleXU=0 Radius=3.5 StartAngle=1.5708 EndAngle=4.71239
    g4: LineSegment StartX=15.5 StartY=3.5 StartZ=0 EndX=-15.5 EndY=3.5 EndZ=0
    g5: LineSegment StartX=-15.5 StartY=-3.5 StartZ=0 EndX=15.5 EndY=-3.5 EndZ=0
  constraints (15):
    c: PointOnObject(g0,g-1)
    c: PointOnObject(g1,g-1)
    c: Equal(g0,g1)
    c: Diameter(g0) = 4.2
    c: Distance(g0,g1) = 31
    c: Distance(g-1,g0) = 15.5
    c: Coincident(g2,g0)
    c: Diameter(g2) = 7
    c: Coincident(g3,g1)
    c: Horizontal(g4)
    c: Tangent(g2,g4) = -1.5708
    c: Tangent(g3,g5) = -1.5708
    c: Coincident(g3,g4)
    c: Tangent(g3,g4,g3) = -1.5708
    c: Tangent(g2,g5) = -1.5708
FEATURE [PartDesign::Pad] Pad016
  BaseFeature = -> Pad015
  Direction = (0,0,1)
  Length = 1
  Length2 = 10
  Profile = -> Sketch036
  ReferenceAxis = -> Sketch036 [N_Axis]
  Reversed = true
  Type = 0
FEATURE [Sketcher::SketchObject] Sketch037
  FullyConstrained = true
  MapMode = 5
  Placement = pos=(0,0,19) rot=(0,0,1;0rad)
  Support = -> [Pad016]
  sketch-geometry (4):
    g0: ArcOfCircle CenterX=0 CenterY=6.5 CenterZ=0 NormalX=0 NormalY=0 NormalZ=1 AngleXU=0 Radius=2.5 StartAngle=2.49809 EndAngle=3.78509
    g1: LineSegment StartX=-2 StartY=8 StartZ=0 EndX=2 EndY=8 EndZ=0
    g2: LineSegment StartX=-2 StartY=5 StartZ=0 EndX=2 EndY=5 EndZ=0
    g3: ArcOfCircle CenterX=0 CenterY=6.5 CenterZ=0 NormalX=0 NormalY=0 NormalZ=1 AngleXU=0 Radius=2.5 StartAngle=5.63968 EndAngle=6.92669
  constraints (13):
    c: PointOnObject(g0,g-2)
    c: Distance(g0,g-1) = 6.5
    c: Diameter(g0) = 5
    c: Horizontal(g1)
    c: Horizontal(g2)
    c: DistanceY(g2,g1) = 3
    c: DistanceY(g0,g1) = 1.5
    c: Coincident(g3,g1)
    c: Coincident(g0,g1)
    c: Equal(g0,g3)
    c: Coincident(g0,g2)
    c: Coincident(g3,g2)
    c: Coincident(g0,g3)
FEATURE [PartDesign::Pad] Pad017
  BaseFeature = -> Pad016
  Direction = (0,0,1)
  Length = 10
  Length2 = 10
  Profile = -> Sketch037
  ReferenceAxis = -> Sketch037 [N_Axis]
  Type = 0
FEATURE [Sketcher::SketchObject] Sketch043  label="Sketch043: Gear aid"
  FullyConstrained = false
  MapMode = 5
  Placement = pos=(0,0,29) rot=(0,0,1;0rad)
  Support = -> [Pad017]
  sketch-geometry (4):
    g0: LineSegment StartX=0 StartY=6.50621 StartZ=0 EndX=0 EndY=57.9462 EndZ=0
    g1: Circle CenterX=0 CenterY=57.9462 CenterZ=0 NormalX=0 NormalY=0 NormalZ=1 AngleXU=0 Radius=22.3949
    g2: Circle CenterX=0 CenterY=6.50621 CenterZ=0 NormalX=0 NormalY=0 NormalZ=1 AngleXU=0 Radius=2.48851
    g3: Circle CenterX=0 CenterY=6.50621 CenterZ=0 NormalX=0 NormalY=0 NormalZ=1 AngleXU=0 Radius=15.9809
  constraints (6):
    c: PointOnObject(g0,g-2)
    c: PointOnObject(g0,g-2)
    c: Coincident(g1,g0)
    c: Coincident(g2,g0)
    c: Distance(g0) = 51.44
    c: Coincident(g3,g0)
FEATURE [PartDesign::Body] Body007  label="Body002: Motor"
  Group = -> [Sketch034,Pad014,Sketch035,Pad015,Sketch036,Pad016,Sketch037,Pad017,Sketch043]
  Origin = -> Origin007
  Placement = pos=(20.0052,-14.8071,-27.2) rot=(0.447214,0.774597,0.447214;1.82348rad)
  Tip = -> Pad017
FEATURE [Sketcher::SketchObject] Sketch062
  AttachmentOffset = pos=(0,0,20) rot=(0,0,1;0rad)
  FullyConstrained = false
  MapMode = 5
  Placement = pos=(20,-4.4e-15,4.4e-15) rot=(0.57735,0.57735,0.57735;2.0944rad)
  Support = -> [YZ_Plane001]
  sketch-geometry (4):
    g0: Circle CenterX=-14.8 CenterY=-27.2 CenterZ=0 NormalX=0 NormalY=0 NormalZ=1 AngleXU=0 Radius=12.5
    g1: LineSegment StartX=0 StartY=0 StartZ=0 EndX=-14.8 EndY=-27.2 EndZ=0
    g2: LineSegment StartX=-14.8 StartY=-27.2 StartZ=0 EndX=-27.7105 EndY=-50.9274 EndZ=0
    g3: Circle CenterX=-16.4728 CenterY=-30.2744 CenterZ=0 NormalX=0 NormalY=0 NormalZ=1 AngleXU=0 Radius=16
  constraints (10):
    c: Distance(g0,g-2) = 14.8
    c: Distance(g0,g-1) = 27.2
    c: Diameter(g0) = 25
    c: Coincident(g1,g-1)
    c: Coincident(g1,g0)
    c: Coincident(g2,g0)
    c: Parallel(g1,g2)
    c: PointOnObject(g3,g2)
    c: Tangent(g3,g0)
    c: Diameter(g3) = 32
FEATURE [Sketcher::SketchObject] Sketch063
  AttachmentOffset = pos=(0,0,-3) rot=(0,0,1;0rad)
  FullyConstrained = true
  MapMode = 5
  Placement = pos=(35,0,1e-15) rot=(0.707107,0,0.707107;3.14159rad)
  sketch-geometry (13):
    g0: Circle CenterX=-10.8627 CenterY=16.7929 CenterZ=0 NormalX=0 NormalY=0 NormalZ=1 AngleXU=0 Radius=1.7
    g1: Circle CenterX=-20 CenterY=0 CenterZ=0 NormalX=0 NormalY=0 NormalZ=1 AngleXU=0 Radius=1.7
    g2: LineSegment StartX=-27.2 StartY=14.8 StartZ=0 EndX=0 EndY=0 EndZ=0
    g3: LineSegment StartX=-10.8627 StartY=16.7929 StartZ=0 EndX=-15.4313 EndY=8.39646 EndZ=0
    g4: LineSegment StartX=-20 StartY=0 StartZ=0 EndX=-15.4313 EndY=8.39646 EndZ=0
    g5: ArcOfCircle CenterX=-20 CenterY=0 CenterZ=0 NormalX=0 NormalY=0 NormalZ=1 AngleXU=0 Radius=3.5 StartAngle=1.5708 EndAngle=4.71239
    g6: ArcOfCircle CenterX=-10.8627 CenterY=16.7929 CenterZ=0 NormalX=0 NormalY=0 NormalZ=1 AngleXU=0 Radius=3.5 StartAngle=0.574165 EndAngle=3.71576
    g7: LineSegment StartX=-20 StartY=3.5 StartZ=0 EndX=-15.6125 EndY=3.5 EndZ=0
    g8: ArcOfCircle CenterX=0 CenterY=0 CenterZ=0 NormalX=0 NormalY=0 NormalZ=1 AngleXU=0 Radius=16 StartAngle=2.92106 EndAngle=3.36213
    g9: ArcOfCircle CenterX=0 CenterY=0 CenterZ=0 NormalX=0 NormalY=0 NormalZ=1 AngleXU=0 Radius=16 StartAngle=1.92443 EndAngle=2.36549
    g10: LineSegment StartX=-13.8014 StartY=14.892 StartZ=0 EndX=-11.4184 EndY=11.208 EndZ=0
    g11: LineSegment StartX=-7.92391 StartY=18.6939 StartZ=0 EndX=-5.54091 EndY=15.0099 EndZ=0
    g12: LineSegment StartX=-20 StartY=-3.5 StartZ=0 EndX=-15.6125 EndY=-3.5 EndZ=0
  constraints (34):
    c: Coincident(g2,g-1)
    c: Distance(g2,g-1) = 14.8
    c: Distance(g2,g-2) = 27.2
    c: Coincident(g3,g0)
    c: PointOnObject(g3,g2)
    c: Coincident(g4,g1)
    c: Coincident(g4,g3)
    c: Perpendicular(g2,g3)
    c: Perpendicular(g4,g2)
    c: Equal(g3,g4)
    c: Diameter(g0) = 3.4
    c: Equal(g0,g1)
    c: PointOnObject(g1,g-1)
    c: Distance(g1,g-2) = 20
    c: Coincident(g5,g1)
    c: Coincident(g6,g0)
    c: Horizontal(g7)
    c: Coincident(g8,g2)
    c: Coincident(g8,g7)
    c: Coincident(g9,g8)
    c: Coincident(g10,g9)
    c: Coincident(g12,g8)
    c: Horizontal(g12)
    c: Diameter(g5) = 7
    c: Equal(g5,g6)
    c: Equal(g10,g12)
    c: Equal(g7,g11)
    c: Equal(g9,g8)
    c: Tangent(g7,g5) = 1.5708
    c: Tangent(g11,g6) = 1.5708
    c: Tangent(g10,g6) = -1.5708
    c: Tangent(g12,g5) = -1.5708
    c: Coincident(g11,g9)
    c: Diameter(g8) = 32
FEATURE [PartDesign::Pad] Pad018
  BaseFeature = -> Fillet
  Direction = (1,0,-2e-16)
  Length = 3
  Length2 = 10
  Placement = pos=(0,0,0) rot=(1,0,0;1.5708rad)
  Profile = -> Sketch063
  ReferenceAxis = -> Sketch063 [N_Axis]
  Reversed = true
  Type = 0
FEATURE [Sketcher::SketchObject] Sketch064
  FullyConstrained = true
  MapMode = 5
  Placement = pos=(0,0,0) rot=(0.57735,0.57735,0.57735;2.0944rad)
  Support = -> [YZ_Plane008]
  sketch-geometry (6):
    g0: Circle CenterX=0 CenterY=0 CenterZ=0 NormalX=0 NormalY=0 NormalZ=1 AngleXU=0 Radius=1.7
    g1: ArcOfCircle CenterX=0 CenterY=0 CenterZ=0 NormalX=0 NormalY=0 NormalZ=1 AngleXU=0 Radius=3.25 StartAngle=6.19048 EndAngle=9.93442
    g2: LineSegment StartX=3.23604 StartY=-0.300876 StartZ=0 EndX=1.84604 EndY=-15.2509 EndZ=0
    g3: ArcOfCircle CenterX=-1.39 CenterY=-14.95 CenterZ=0 NormalX=0 NormalY=0 NormalZ=1 AngleXU=0 Radius=3.25 StartAngle=2.44653 EndAngle=6.19048
    g4: ArcOfCircle CenterX=-11.5662 CenterY=-6.46424 CenterZ=0 NormalX=0 NormalY=0 NormalZ=1 AngleXU=0 Radius=10 StartAngle=5.58812 EndAngle=6.79283
    g5: Circle CenterX=-1.39 CenterY=-14.95 CenterZ=0 NormalX=0 NormalY=0 NormalZ=1 AngleXU=0 Radius=2.15
  constraints (14):
    c: Diameter(g0) = 3.4
    c: Coincident(g1,g0)
    c: Diameter(g1) = 6.5
    c: Coincident(g0,g-1)
    c: Distance(g3,g-1) = 14.95
    c: Diameter(g3) = 6.5
    c: Distance(g3,g-2) = 1.39
    c: Coincident(g5,g3)
    c: Diameter(g5) = 4.3
    c: Diameter(g4) = 20
    c: Tangent(g1,g4) = 1.5708
    c: Tangent(g1,g2) = 1.5708
    c: Tangent(g3,g2) = 1.5708
    c: Tangent(g3,g4) = 1.5708
FEATURE [PartDesign::Pad] Pad019
  Direction = (1,-2e-16,3e-16)
  Length = 3
  Length2 = 10
  Placement = pos=(0,0,0) rot=(0.57735,0.57735,0.57735;2.0944rad)
  Profile = -> Sketch064
  ReferenceAxis = -> Sketch064 [N_Axis]
  Type = 0
FEATURE [PartDesign::Body] Body008  label="Body008: Motor link A v0"
  Group = -> [Sketch064,Pad019]
  Origin = -> Origin008
  Placement = pos=(35,0,-20) rot=(0,0,1;0rad)
  Tip = -> Pad019
FEATURE [Sketcher::SketchObject] Sketch065
  FullyConstrained = true
  MapMode = 5
  Placement = pos=(0,0,0) rot=(0.57735,0.57735,0.57735;2.0944rad)
  Support = -> [YZ_Plane009]
  sketch-geometry (6):
    g0: Circle CenterX=0 CenterY=0 CenterZ=0 NormalX=0 NormalY=0 NormalZ=1 AngleXU=0 Radius=1.7
    g1: ArcOfCircle CenterX=0 CenterY=0 CenterZ=0 NormalX=0 NormalY=0 NormalZ=1 AngleXU=0 Radius=3.5 StartAngle=6.14586 EndAngle=9.88376
    g2: LineSegment StartX=3.46705 StartY=-0.479131 StartZ=0 EndX=1.5094 EndY=-14.6449 EndZ=0
    g3: ArcOfCircle CenterX=-1.71 CenterY=-14.2 CenterZ=0 NormalX=0 NormalY=0 NormalZ=1 AngleXU=0 Radius=3.25 StartAngle=2.47246 EndAngle=6.14586
    g4: ArcOfCircle CenterX=-12.1028 CenterY=-5.98099 CenterZ=0 NormalX=0 NormalY=0 NormalZ=1 AngleXU=0 Radius=10 StartAngle=5.61406 EndAngle=6.74217
    g5: Circle CenterX=-1.71 CenterY=-14.2 CenterZ=0 NormalX=0 NormalY=0 NormalZ=1 AngleXU=0 Radius=2.15
  constraints (14):
    c: Diameter(g0) = 3.4
    c: Coincident(g1,g0)
    c: Diameter(g1) = 7
    c: Coincident(g0,g-1)
    c: Diameter(g3) = 6.5
    c: Coincident(g5,g3)
    c: Diameter(g5) = 4.3
    c: Diameter(g4) = 20
    c: Tangent(g1,g4) = 1.5708
    c: Tangent(g1,g2) = 1.5708
    c: Tangent(g3,g2) = 1.5708
    c: Tangent(g3,g4) = 1.5708
    c: Distance(g3,g-2) = 1.71
    c: Distance(g3,g-1) = 14.2
FEATURE [PartDesign::Pad] Pad020
  Direction = (1,-2e-16,3e-16)
  Length = 3
  Length2 = 10
  Placement = pos=(0,0,0) rot=(0.57735,0.57735,0.57735;2.0944rad)
  Profile = -> Sketch065
  ReferenceAxis = -> Sketch065 [N_Axis]
  Type = 0
FEATURE [PartDesign::Body] Body009  label="Body008: Motor link B v0"
  Group = -> [Sketch065,Pad020]
  Origin = -> Origin009
  Placement = pos=(38,-16.7835,-10.875) rot=(0,0.5,0.866025;3.14159rad)
  Tip = -> Pad020
FEATURE [Part::Part2DObjectPython] InvoluteGear  # Draft 2D object (typed FeaturePython)
  ExternalGear = true
  HighPrecision = true
  Modules = 1
  NumberOfTeeth = 10
  PressureAngle = 20
FEATURE [Part::Part2DObjectPython] InvoluteGear002  # Draft 2D object (typed FeaturePython)
  ExternalGear = true
  HighPrecision = true
  Modules = 1
  NumberOfTeeth = 39
  PressureAngle = 20
FEATURE [PartDesign::Pad] Pad021
  Direction = (0,0,1)
  Length = 8
  Length2 = 10
  Profile = -> InvoluteGear
  ReferenceAxis = -> InvoluteGear [N_Axis]
  Type = 0
FEATURE [PartDesign::Pad] Pad033
  Direction = (0,0,1)
  Length = 9
  Length2 = 10
  Profile = -> InvoluteGear002
  ReferenceAxis = -> InvoluteGear002 [N_Axis]
  Type = 0
FEATURE [Sketcher::SketchObject] Sketch045
  FullyConstrained = true
  MapMode = 5
  Support = -> [XY_Plane010]
  sketch-geometry (4):
    g0: ArcOfCircle CenterX=0 CenterY=0 CenterZ=0 NormalX=0 NormalY=0 NormalZ=1 AngleXU=0 Radius=2.675 StartAngle=2.46496 EndAngle=3.81822
    g1: LineSegment StartX=-2.08567 StartY=1.675 StartZ=0 EndX=2.08567 EndY=1.675 EndZ=0
    g2: LineSegment StartX=-2.08567 StartY=-1.675 StartZ=0 EndX=2.08567 EndY=-1.675 EndZ=0
    g3: ArcOfCircle CenterX=0 CenterY=0 CenterZ=0 NormalX=0 NormalY=0 NormalZ=1 AngleXU=0 Radius=2.675 StartAngle=5.60656 EndAngle=6.95981
  constraints (12):
    c: Coincident(g0,g-1)
    c: Diameter(g0) = 5.35
    c: Horizontal(g1)
    c: Horizontal(g2)
    c: Equal(g1,g2)
    c: Distance(g1,g2) = 3.35
    c: Coincident(g3,g1)
    c: Coincident(g0,g1)
    c: Equal(g0,g3)
    c: Coincident(g0,g2)
    c: Coincident(g3,g2)
    c: Coincident(g0,g3)
FEATURE [PartDesign::Pocket] Pocket011
  BaseFeature = -> Pad021
  Direction = (0,0,-1)
  Length = 5
  Length2 = 5
  Profile = -> Sketch045
  ReferenceAxis = -> Sketch045 [N_Axis]
  Reversed = true
  Type = 1
FEATURE [PartDesign::Body] Body010  label="Body008: Pinion"
  Group = -> [InvoluteGear,Pad021,Sketch045,Pocket011]
  Origin = -> Origin010
  Placement = pos=(41.6153,-11.97,-21.5) rot=(0,1,0;1.5708rad)
  Tip = -> Pocket011
FEATURE [Sketcher::SketchObject] Sketch077
  FullyConstrained = true
  MapMode = 5
  Support = -> [XY_Plane013]
  sketch-geometry (9):
    g0: ArcOfCircle CenterX=0 CenterY=0 CenterZ=0 NormalX=0 NormalY=0 NormalZ=1 AngleXU=0 Radius=4.15 StartAngle=0.813792 EndAngle=5.46939
    g1: LineSegment StartX=2.85 StartY=3.01662 StartZ=0 EndX=2.85 EndY=0.85 EndZ=0
    g2: LineSegment StartX=2.85 StartY=0.85 StartZ=0 EndX=1.55 EndY=0.85 EndZ=0
    g3: LineSegment StartX=1.55 StartY=0.85 StartZ=0 EndX=1.55 EndY=-0.85 EndZ=0
    g4: LineSegment StartX=1.55 StartY=-0.85 StartZ=0 EndX=2.85 EndY=-0.85 EndZ=0
    g5: LineSegment StartX=2.85 StartY=-0.85 StartZ=0 EndX=2.85 EndY=-3.01662 EndZ=0
    g6: LineSegment StartX=1.55 StartY=0 StartZ=0 EndX=-4.15 EndY=0 EndZ=0
    g7: LineSegment StartX=2.85 StartY=0.85 StartZ=0 EndX=2.85 EndY=-0.85 EndZ=0
    g8: LineSegment StartX=2.85 StartY=0 StartZ=0 EndX=-4.15 EndY=0 EndZ=0
  constraints (27):
    c: Coincident(g0,g-1)
    c: Vertical(g1)
    c: Coincident(g2,g1)
    c: Horizontal(g2)
    c: Coincident(g3,g2)
    c: Vertical(g3)
    c: Horizontal(g4)
    c: Coincident(g5,g4)
    c: Vertical(g5)
    c: Diameter(g0) = 8.3
    c: Coincident(g0,g5)
    c: Coincident(g0,g1)
    c: PointOnObject(g6,g3)
    c: PointOnObject(g6,g0)
    c: Horizontal(g6)
    c: Perpendicular(g0,g6)
    c: Distance(g6) = 5.7
    c: Coincident(g7,g1)
    c: Coincident(g7,g4)
    c: Vertical(g7)
    c: PointOnObject(g8,g7)
    c: Coincident(g8,g6)
    c: Horizontal(g8)
    c: Distance(g8) = 7
    c: Equal(g1,g5)
    c: Coincident(g3,g4)
    c: Distance(g7) = 1.7
FEATURE [PartDesign::Pocket] Pocket022
  BaseFeature = -> Pad033
  Direction = (0,0,-1)
  Length = 5
  Length2 = 5
  Profile = -> Sketch077
  ReferenceAxis = -> Sketch077 [N_Axis]
  Reversed = true
  Type = 1
FEATURE [PartDesign::Body] Body013  label="Body009: Gear v001"
  Group = -> [InvoluteGear002,Pad033,Sketch077,Pocket022]
  Origin = -> Origin013
  Placement = pos=(40,0,-9e-15) rot=(0.57735,0.57735,0.57735;2.0944rad)
  Tip = -> Pocket022
FEATURE [Sketcher::SketchObject] Sketch027
  FullyConstrained = false
  MapMode = 5
  Support = -> [XY_Plane005]
  sketch-geometry (1):
    g0: Circle CenterX=0 CenterY=0 CenterZ=0 NormalX=0 NormalY=0 NormalZ=1 AngleXU=0 Radius=7
  constraints (1):
    c: Diameter(g0) = 14
FEATURE [Sketcher::SketchObject] Sketch028
  AttachmentOffset = pos=(0,0,12) rot=(0,0,1;0rad)
  FullyConstrained = true
  MapMode = 5
  Placement = pos=(0,0,12) rot=(0,0,1;0rad)
  Support = -> [XY_Plane005]
  sketch-geometry (1):
    g0: Circle CenterX=0 CenterY=0 CenterZ=0 NormalX=0 NormalY=0 NormalZ=1 AngleXU=0 Radius=6
  constraints (2):
    c: Coincident(g0,g-1)
    c: Diameter(g0) = 12
FEATURE [PartDesign::AdditiveLoft] AdditiveLoft
  Closed = false
  Profile = -> Sketch028
  Ruled = false
  Sections = -> [Sketch027]
FEATURE [Sketcher::SketchObject] Sketch029
  FullyConstrained = true
  MapMode = 5
  Placement = pos=(0,0,0) rot=(0.57735,0.57735,0.57735;2.0944rad)
  Support = -> [YZ_Plane005]
  sketch-geometry (6):
    g0: LineSegment StartX=0 StartY=12 StartZ=0 EndX=46.8295 EndY=8 EndZ=0
    g1: LineSegment StartX=0 StartY=0 StartZ=0 EndX=50 EndY=0 EndZ=0
    g2: LineSegment StartX=46.8295 StartY=8 StartZ=0 EndX=50 EndY=0 EndZ=0
    g3: LineSegment StartX=0 StartY=0 StartZ=0 EndX=-50 EndY=0 EndZ=0
    g4: LineSegment StartX=-50 StartY=0 StartZ=0 EndX=-46.8295 EndY=8 EndZ=0
    g5: LineSegment StartX=-46.8295 StartY=8 StartZ=0 EndX=0 EndY=12 EndZ=0
  constraints (17):
    c: PointOnObject(g0,g-2)
    c: Coincident(g1,g-1)
    c: PointOnObject(g1,g-1)
    c: Coincident(g2,g0)
    c: Coincident(g2,g1)
    c: Coincident(g3,g1)
    c: PointOnObject(g3,g-1)
    c: Coincident(g4,g3)
    c: Coincident(g5,g4)
    c: Coincident(g5,g0)
    c: Equal(g1,g3)
    c: Equal(g4,g2)
    c: Equal(g0,g5)
    c: Distance(g1) = 50
    c: Distance(g0) = 47
    c: Distance(g0,g1) = 12
    c: Distance(g0,g1) = 8
FEATURE [PartDesign::Pad] Pad010
  BaseFeature = -> AdditiveLoft
  Direction = (1,-2e-16,3e-16)
  Length = 5
  Length2 = 10
  Midplane = true
  Profile = -> Sketch029
  ReferenceAxis = -> Sketch029 [N_Axis]
  Type = 0
FEATURE [PartDesign::Fillet] Fillet002
  Base = -> Pad010 [Edge1]
  BaseFeature = -> Pad010
  Radius = 0.5
  SupportTransform = false
  UseAllEdges = false
FEATURE [PartDesign::Fillet] Fillet003
  Base = -> Fillet002 [Edge13,Edge6,Edge8]
  BaseFeature = -> Fillet002
  Radius = 0.5
  SupportTransform = false
  UseAllEdges = false
FEATURE [PartDesign::Fillet] Fillet004
  Base = -> Fillet003 [Edge25,Edge28,Edge40,Edge35,Edge41,Edge57,Edge44,Edge36,Edge24,Edge29,Edge34,Edge54]
  BaseFeature = -> Fillet003
  Radius = 0.5
  SupportTransform = false
  UseAllEdges = false
FEATURE [Sketcher::SketchObject] Sketch030
  FullyConstrained = true
  MapMode = 5
  Support = -> [XY_Plane005]
  sketch-geometry (10):
    g0: Circle CenterX=0 CenterY=0 CenterZ=0 NormalX=0 NormalY=0 NormalZ=1 AngleXU=0 Radius=4
    g1: LineSegment StartX=2.8 StartY=2.85657 StartZ=0 EndX=2.8 EndY=0.85 EndZ=0
    g2: LineSegment StartX=2.8 StartY=0.85 StartZ=0 EndX=1.5 EndY=0.85 EndZ=0
    g3: LineSegment StartX=1.5 StartY=0.85 StartZ=0 EndX=1.5 EndY=-0.85 EndZ=0
    g4: LineSegment StartX=1.5 StartY=-0.85 StartZ=0 EndX=2.8 EndY=-0.85 EndZ=0
    g5: LineSegment StartX=2.8 StartY=-0.85 StartZ=0 EndX=2.8 EndY=-2.85657 EndZ=0
    g6: ArcOfCircle CenterX=0 CenterY=0 CenterZ=0 NormalX=0 NormalY=0 NormalZ=1 AngleXU=0 Radius=4 StartAngle=0.795399 EndAngle=5.48779
    g7: LineSegment StartX=-4 StartY=0 StartZ=0 EndX=1.5 EndY=0 EndZ=0
    g8: LineSegment StartX=2.8 StartY=0.85 StartZ=0 EndX=2.8 EndY=-0.85 EndZ=0
    g9: LineSegment StartX=2.8 StartY=0 StartZ=0 EndX=-4 EndY=0 EndZ=0
  constraints (29):
    c: Coincident(g0,g-1)
    c: Diameter(g0) = 8
    c: Vertical(g1)
    c: Coincident(g2,g1)
    c: Horizontal(g2)
    c: Vertical(g3)
    c: Coincident(g4,g3)
    c: Horizontal(g4)
    c: Coincident(g5,g4)
    c: PointOnObject(g5,g0)
    c: Vertical(g5)
    c: Equal(g1,g5)
    c: Coincident(g2,g3)
    c: Equal(g2,g4)
    c: Coincident(g6,g0)
    c: Coincident(g6,g5)
    c: Coincident(g6,g1)
    c: PointOnObject(g7,g6)
    c: PointOnObject(g7,g3)
    c: Horizontal(g7)
    c: Perpendicular(g0,g7)
    c: Distance(g7) = 5.5
    c: Distance(g3) = 1.7
    c: Coincident(g8,g1)
    c: Coincident(g8,g4)
    c: PointOnObject(g9,g8)
    c: Coincident(g9,g7)
    c: Horizontal(g9)
    c: Distance(g9) = 6.8
FEATURE [PartDesign::Pocket] Pocket009
  BaseFeature = -> Fillet004
  Direction = (0,0,-1)
  Length = 8
  Length2 = 5
  Profile = -> Sketch030
  ReferenceAxis = -> Sketch030 [N_Axis]
  Reversed = true
  Type = 0
FEATURE [PartDesign::Body] Body005  label="Body005: Handle"
  Group = -> [Sketch027,Sketch028,AdditiveLoft,Sketch029,Pad010,Fillet002,Fillet003,Fillet004,Sketch030,Pocket009]
  Origin = -> Origin005
  Placement = pos=(53.5,0,-1.4e-14) rot=(0.57735,0.57735,0.57735;2.0944rad)
  Tip = -> Pocket009
FEATURE [PartDesign::Pad] Pad034
  BaseFeature = -> Pad018
  Direction = (0,-1,2e-16)
  Length = 10
  Length2 = 10
  Placement = pos=(0,0,0) rot=(1,0,0;1.5708rad)
  Profile = -> Pad018 [Face7]
  Type = 0
FEATURE [Sketcher::SketchObject] Sketch078
  FullyConstrained = true
  MapMode = 5
  Placement = pos=(0,-32.1,1.42e-14) rot=(1,0,0;1.5708rad)
  Support = -> [Pad034]
  sketch-geometry (2):
    g0: Circle CenterX=0 CenterY=0 CenterZ=0 NormalX=0 NormalY=0 NormalZ=1 AngleXU=0 Radius=22.4
    g1: Circle CenterX=0 CenterY=0 CenterZ=0 NormalX=0 NormalY=0 NormalZ=1 AngleXU=0 Radius=25.1
  constraints (4):
    c: Coincident(g0,g-1)
    c: Coincident(g1,g0)
    c: Diameter(g1) = 50.2
    c: Diameter(g0) = 44.8
FEATURE [PartDesign::Pad] Pad035
  BaseFeature = -> Pad034
  Direction = (0,-1,2e-16)
  Length = 20
  Length2 = 10
  Placement = pos=(0,0,0) rot=(1,0,0;1.5708rad)
  Profile = -> Sketch078
  ReferenceAxis = -> Sketch078 [N_Axis]
  Type = 0
FEATURE [PartDesign::Pocket] Pocket023
  BaseFeature = -> Pad035
  Direction = (-1,2e-16,-3e-16)
  Length = 5
  Length2 = 5
  Placement = pos=(0,0,0) rot=(1,0,0;1.5708rad)
  Profile = -> Sketch062
  ReferenceAxis = -> Sketch062 [N_Axis]
  Reversed = true
  Type = 1
FEATURE [PartDesign::Body] Body001  label="Body001: Housing v0"
  Group = -> [Sketch002,Pad001,Sketch004,Revolution,Sketch006,Pocket001,Sketch007,Pocket002,Sketch008,Pocket003,Sketch012,Revolution001,Sketch013,Pocket,Sketch014,Pocket004,Sketch015,Pocket005,Sketch016,Pocket006,Sketch060,Pad008,Fillet,Sketch061,Sketch062,Sketch063,Pad018,Pad034,Sketch078,Pad035,Pocket023]
  Origin = -> Origin001
  Tip = -> Pocket023
FEATURE [Sketcher::SketchObject] Sketch079
  FullyConstrained = true
  MapMode = 5
  Placement = pos=(0,0,0) rot=(1,0,0;1.5708rad)
  Support = -> [XZ_Plane014]
  sketch-geometry (1):
    g0: Circle CenterX=0 CenterY=0 CenterZ=0 NormalX=0 NormalY=0 NormalZ=1 AngleXU=0 Radius=26
  constraints (2):
    c: Coincident(g0,g-1)
    c: Diameter(g0) = 52
FEATURE [PartDesign::Pad] Pad036
  Direction = (0,-1,2e-16)
  Length = 32
  Length2 = 16
  Placement = pos=(0,0,0) rot=(1,0,0;1.5708rad)
  Profile = -> Sketch079
  ReferenceAxis = -> Sketch079 [N_Axis]
  Type = 4
FEATURE [Sketcher::SketchObject] Sketch080
  AttachmentOffset = pos=(0,0,38) rot=(0,0,1;0rad)
  FullyConstrained = true
  MapMode = 5
  Placement = pos=(38,-8.4e-15,8.4e-15) rot=(0.57735,0.57735,0.57735;2.0944rad)
  Support = -> [YZ_Plane014]
  sketch-geometry (1):
    g0: Circle CenterX=0 CenterY=0 CenterZ=0 NormalX=0 NormalY=0 NormalZ=1 AngleXU=0 Radius=15.9
  constraints (2):
    c: Coincident(g0,g-1)
    c: Diameter(g0) = 31.8
FEATURE [PartDesign::Pad] Pad037
  BaseFeature = -> Pad036
  Direction = (1,-2e-16,3e-16)
  Length = 10
  Length2 = 10
  Placement = pos=(0,0,0) rot=(1,0,0;1.5708rad)
  Profile = -> Sketch080
  ReferenceAxis = -> Sketch080 [N_Axis]
  Reversed = true
  Type = 2
FEATURE [Sketcher::SketchObject] Sketch081
  AttachmentOffset = pos=(0,0,-34) rot=(0,0,1;0rad)
  FullyConstrained = true
  MapMode = 5
  Placement = pos=(-34,7.5e-15,-7.5e-15) rot=(0.57735,0.57735,0.57735;2.0944rad)
  Support = -> [YZ_Plane014]
  sketch-geometry (1):
    g0: Circle CenterX=0 CenterY=0 CenterZ=0 NormalX=0 NormalY=0 NormalZ=1 AngleXU=0 Radius=15.9
  constraints (2):
    c: Coincident(g0,g-1)
    c: Diameter(g0) = 31.8
FEATURE [PartDesign::Pad] Pad038
  BaseFeature = -> Pad037
  Direction = (1,-2e-16,3e-16)
  Length = 10
  Length2 = 10
  Placement = pos=(0,0,0) rot=(1,0,0;1.5708rad)
  Profile = -> Sketch081
  ReferenceAxis = -> Sketch081 [N_Axis]
  Type = 2
FEATURE [Sketcher::SketchObject] Sketch082
  FullyConstrained = true
  MapMode = 5
  Placement = pos=(0,0,0) rot=(1,0,0;1.5708rad)
  Support = -> [XZ_Plane014]
  sketch-geometry (1):
    g0: Circle CenterX=0 CenterY=0 CenterZ=0 NormalX=0 NormalY=0 NormalZ=1 AngleXU=0 Radius=22.4
  constraints (2):
    c: Coincident(g0,g-1)
    c: Diameter(g0) = 44.8
FEATURE [PartDesign::Pocket] Pocket024
  BaseFeature = -> Pad038
  Direction = (0,1,-2e-16)
  Length = 5
  Length2 = 5
  Midplane = true
  Placement = pos=(0,0,0) rot=(1,0,0;1.5708rad)
  Profile = -> Sketch082
  ReferenceAxis = -> Sketch082 [N_Axis]
  Type = 1
FEATURE [Sketcher::SketchObject] Sketch083
  FullyConstrained = true
  MapMode = 5
  Placement = pos=(-34,5.1e-15,-8.8e-15) rot=(0.707107,0,-0.707107;3.14159rad)
  Support = -> [Pocket024]
  sketch-geometry (1):
    g0: Circle CenterX=0 CenterY=0 CenterZ=0 NormalX=0 NormalY=0 NormalZ=1 AngleXU=0 Radius=12.15
  constraints (2):
    c: Coincident(g0,g-1)
    c: Diameter(g0) = 24.3
FEATURE [PartDesign::Pocket] Pocket025
  BaseFeature = -> Pocket024
  Direction = (1,-1e-16,2e-16)
  Length = 10
  Length2 = 5
  Placement = pos=(0,0,0) rot=(1,0,0;1.5708rad)
  Profile = -> Sketch083
  ReferenceAxis = -> Sketch083 [N_Axis]
  Type = 0
FEATURE [Sketcher::SketchObject] Sketch084
  FullyConstrained = true
  MapMode = 5
  Placement = pos=(-24,0,0) rot=(0.707107,0,-0.707107;3.14159rad)
  Support = -> [Pocket025]
  sketch-geometry (1):
    g0: Circle CenterX=0 CenterY=0 CenterZ=0 NormalX=0 NormalY=0 NormalZ=1 AngleXU=0 Radius=10.5
  constraints (2):
    c: Coincident(g0,g-1)
    c: Diameter(g0) = 21
FEATURE [PartDesign::Pocket] Pocket026
  BaseFeature = -> Pocket025
  Direction = (1,0,2e-16)
  Length = 1
  Length2 = 5
  Placement = pos=(0,0,0) rot=(1,0,0;1.5708rad)
  Profile = -> Sketch084
  ReferenceAxis = -> Sketch084 [N_Axis]
  Type = 0
FEATURE [Sketcher::SketchObject] Sketch085
  FullyConstrained = true
  MapMode = 5
  Placement = pos=(-23,0,-5.3e-15) rot=(0.707107,0,-0.707107;3.14159rad)
  Support = -> [Pocket026]
  sketch-geometry (1):
    g0: Circle CenterX=0 CenterY=0 CenterZ=0 NormalX=0 NormalY=0 NormalZ=1 AngleXU=0 Radius=4.3
  constraints (2):
    c: Coincident(g0,g-1)
    c: Diameter(g0) = 8.6
FEATURE [PartDesign::Pocket] Pocket027
  BaseFeature = -> Pocket026
  Direction = (1,0,2e-16)
  Length = 10
  Length2 = 5
  Placement = pos=(0,0,0) rot=(1,0,0;1.5708rad)
  Profile = -> Sketch085
  ReferenceAxis = -> Sketch085 [N_Axis]
  Type = 0
FEATURE [Sketcher::SketchObject] Sketch086
  FullyConstrained = true
  MapMode = 5
  Placement = pos=(38,-5.7e-15,9.9e-15) rot=(0.707107,0,0.707107;3.14159rad)
  Support = -> [Pocket027]
  sketch-geometry (1):
    g0: Circle CenterX=0 CenterY=0 CenterZ=0 NormalX=0 NormalY=0 NormalZ=1 AngleXU=0 Radius=12.15
  constraints (2):
    c: Coincident(g0,g-1)
    c: Diameter(g0) = 24.3
FEATURE [PartDesign::Pocket] Pocket028
  BaseFeature = -> Pocket027
  Direction = (-1,1e-16,-2e-16)
  Length = 9
  Length2 = 5
  Placement = pos=(0,0,0) rot=(1,0,0;1.5708rad)
  Profile = -> Sketch086
  ReferenceAxis = -> Sketch086 [N_Axis]
  Type = 0
FEATURE [Sketcher::SketchObject] Sketch087
  FullyConstrained = true
  MapMode = 5
  Placement = pos=(29,0,0) rot=(0.707107,0,0.707107;3.14159rad)
  Support = -> [Pocket028]
  sketch-geometry (1):
    g0: Circle CenterX=0 CenterY=0 CenterZ=0 NormalX=0 NormalY=0 NormalZ=1 AngleXU=0 Radius=10.5
  constraints (2):
    c: Coincident(g0,g-1)
    c: Diameter(g0) = 21
FEATURE [PartDesign::Pocket] Pocket029
  BaseFeature = -> Pocket028
  Direction = (-1,0,-2e-16)
  Length = 1
  Length2 = 5
  Placement = pos=(0,0,0) rot=(1,0,0;1.5708rad)
  Profile = -> Sketch087
  ReferenceAxis = -> Sketch087 [N_Axis]
  Type = 0
FEATURE [Sketcher::SketchObject] Sketch088
  FullyConstrained = true
  MapMode = 5
  Placement = pos=(28,0,6.4e-15) rot=(0.707107,0,0.707107;3.14159rad)
  Support = -> [Pocket029]
  sketch-geometry (1):
    g0: Circle CenterX=0 CenterY=0 CenterZ=0 NormalX=0 NormalY=0 NormalZ=1 AngleXU=0 Radius=4.3
  constraints (2):
    c: Coincident(g0,g-1)
    c: Diameter(g0) = 8.6
FEATURE [PartDesign::Pocket] Pocket030
  BaseFeature = -> Pocket029
  Direction = (-1,0,-2e-16)
  Length = 10
  Length2 = 5
  Placement = pos=(0,0,0) rot=(1,0,0;1.5708rad)
  Profile = -> Sketch088
  ReferenceAxis = -> Sketch088 [N_Axis]
  Type = 0
FEATURE [Sketcher::SketchObject] Sketch089
  FullyConstrained = true
  MapMode = 5
  Placement = pos=(38,-5.7e-15,9.9e-15) rot=(0.707107,0,0.707107;3.14159rad)
  Support = -> [Pocket030]
  sketch-geometry (8):
    g0: ArcOfCircle CenterX=0 CenterY=0 CenterZ=0 NormalX=0 NormalY=0 NormalZ=1 AngleXU=0 Radius=15.9 StartAngle=1.74143 EndAngle=1.93306
    g1: ArcOfCircle CenterX=0 CenterY=0 CenterZ=0 NormalX=0 NormalY=0 NormalZ=1 AngleXU=0 Radius=20.15 StartAngle=1.7052 EndAngle=1.85422
    g2: LineSegment StartX=-2.7 StartY=19.9683 StartZ=0 EndX=-2.7 EndY=15.6691 EndZ=0
    g3: LineSegment StartX=-5.63477 StartY=14.8681 StartZ=0 EndX=-5.63477 EndY=19.3461 EndZ=0
    g4: LineSegment StartX=15.6691 StartY=-2.7 StartZ=0 EndX=19.9683 EndY=-2.7 EndZ=0
    g5: LineSegment StartX=14.8681 StartY=-5.63477 StartZ=0 EndX=19.3461 EndY=-5.63477 EndZ=0
    g6: ArcOfCircle CenterX=0 CenterY=0 CenterZ=0 NormalX=0 NormalY=0 NormalZ=1 AngleXU=0 Radius=15.9 StartAngle=5.92093 EndAngle=6.11255
    g7: ArcOfCircle CenterX=0 CenterY=0 CenterZ=0 NormalX=0 NormalY=0 NormalZ=1 AngleXU=0 Radius=20.15 StartAngle=5.99976 EndAngle=6.14879
  constraints (24):
    c: Coincident(g0,g-1)
    c: Coincident(g1,g0)
    c: Coincident(g2,g1)
    c: Coincident(g2,g0)
    c: Vertical(g2)
    c: Coincident(g3,g0)
    c: Coincident(g3,g1)
    c: Vertical(g3)
    c: Distance(g0,g-2) = 2.7
    c: Distance(g1,g1) = 3
    c: Diameter(g1) = 40.3
    c: Diameter(g0) = 31.8
    c: Horizontal(g4)
    c: Horizontal(g5)
    c: Coincident(g6,g0)
    c: Coincident(g6,g5)
    c: Coincident(g6,g4)
    c: Coincident(g7,g0)
    c: Coincident(g7,g5)
    c: Coincident(g7,g4)
    c: Equal(g6,g0)
    c: Equal(g3,g5)
    c: Equal(g2,g4)
    c: Equal(g1,g7)
FEATURE [PartDesign::Pad] Pad039
  BaseFeature = -> Pocket030
  Direction = (1,-1e-16,2e-16)
  Length = 5
  Length2 = 10
  Placement = pos=(0,0,0) rot=(1,0,0;1.5708rad)
  Profile = -> Sketch089
  ReferenceAxis = -> Sketch089 [N_Axis]
  Reversed = true
  Type = 0
FEATURE [Sketcher::SketchObject] Sketch090
  AttachmentOffset = pos=(0,0,-3) rot=(0,0,1;0rad)
  FullyConstrained = true
  MapMode = 5
  Placement = pos=(35,-5.2e-15,9.2e-15) rot=(0.707107,0,0.707107;3.14159rad)
  Support = -> [Pad039]
  sketch-geometry (14):
    g0: LineSegment StartX=-27.2 StartY=14.4 StartZ=0 EndX=0 EndY=0 EndZ=0
    g1: LineSegment StartX=-15.318 StartY=8.10951 StartZ=0 EndX=-20 EndY=0 EndZ=0
    g2: LineSegment StartX=-15.318 StartY=8.10951 StartZ=0 EndX=-10.6359 EndY=16.219 EndZ=0
    g3: Circle CenterX=-20 CenterY=0 CenterZ=0 NormalX=0 NormalY=0 NormalZ=1 AngleXU=0 Radius=1.7
    g4: Circle CenterX=-10.6359 CenterY=16.219 CenterZ=0 NormalX=0 NormalY=0 NormalZ=1 AngleXU=0 Radius=1.7
    g5: ArcOfCircle CenterX=-20 CenterY=0 CenterZ=0 NormalX=0 NormalY=0 NormalZ=1 AngleXU=0 Radius=3.5 StartAngle=1.5708 EndAngle=4.71239
    g6: ArcOfCircle CenterX=-10.6359 CenterY=16.219 CenterZ=0 NormalX=0 NormalY=0 NormalZ=1 AngleXU=0 Radius=3.5 StartAngle=0.58042 EndAngle=3.72201
    g7: ArcOfCircle CenterX=0 CenterY=0 CenterZ=0 NormalX=0 NormalY=0 NormalZ=1 AngleXU=0 Radius=15.9 StartAngle=1.92927 EndAngle=2.37316
    g8: ArcOfCircle CenterX=0 CenterY=0 CenterZ=0 NormalX=0 NormalY=0 NormalZ=1 AngleXU=0 Radius=15.9 StartAngle=2.91965 EndAngle=3.36354
    g9: LineSegment StartX=-20 StartY=3.5 StartZ=0 EndX=-15.51 EndY=3.5 EndZ=0
    g10: LineSegment StartX=-20 StartY=-3.5 StartZ=0 EndX=-15.51 EndY=-3.5 EndZ=0
    g11: LineSegment StartX=-13.5628 StartY=14.2997 StartZ=0 EndX=-11.4321 EndY=11.0506 EndZ=0
    g12: LineSegment StartX=-5.57849 StartY=14.8893 StartZ=0 EndX=-7.70913 EndY=18.1383 EndZ=0
    g13: LineSegment StartX=-10.6359 StartY=16.219 StartZ=0 EndX=0 EndY=0 EndZ=0
  constraints (36):
    c: Coincident(g0,g-1)
    c: Distance(g0,g-1) = 14.4
    c: Distance(g0,g-2) = 27.2
    c: PointOnObject(g1,g0)
    c: PointOnObject(g1,g-1)
    c: Coincident(g2,g1)
    c: Parallel(g2,g1)
    c: Coincident(g3,g1)
    c: Coincident(g4,g2)
    c: Diameter(g3) = 3.4
    c: Diameter(g4) = 3.4
    c: Distance(g3,g0) = 20
    c: Angle(g-1,g1) = 1.0472
    c: Equal(g2,g1)
    c: Coincident(g5,g3)
    c: Coincident(g6,g4)
    c: Coincident(g7,g0)
    c: Coincident(g8,g7)
    c: Diameter(g8) = 31.8
    c: Equal(g8,g7)
    c: Coincident(g9,g8)
    c: Horizontal(g9)
    c: Coincident(g10,g8)
    c: Horizontal(g10)
    c: Diameter(g5) = 7
    c: Tangent(g9,g5) = 1.5708
    c: Tangent(g10,g5) = -1.5708
    c: Coincident(g11,g7)
    c: Coincident(g12,g7)
    c: Coincident(g13,g4)
    c: Coincident(g13,g7)
    c: Parallel(g13,g12)
    c: Parallel(g13,g11)
    c: Tangent(g12,g6) = -1.5708
    c: Tangent(g11,g6) = -1.5708
    c: Equal(g6,g5)
FEATURE [Sketcher::SketchObject] Sketch091
  FullyConstrained = true
  MapMode = 5
  Placement = pos=(0,0,0) rot=(0.57735,0.57735,0.57735;2.0944rad)
  Support = -> [YZ_Plane015]
  sketch-geometry (6):
    g0: Circle CenterX=0 CenterY=0 CenterZ=0 NormalX=0 NormalY=0 NormalZ=1 AngleXU=0 Radius=1.7
    g1: ArcOfCircle CenterX=0 CenterY=0 CenterZ=0 NormalX=0 NormalY=0 NormalZ=1 AngleXU=0 Radius=3.25 StartAngle=6.19048 EndAngle=9.93442
    g2: LineSegment StartX=3.23604 StartY=-0.300876 StartZ=0 EndX=1.84604 EndY=-15.2509 EndZ=0
    g3: ArcOfCircle CenterX=-1.39 CenterY=-14.95 CenterZ=0 NormalX=0 NormalY=0 NormalZ=1 AngleXU=0 Radius=3.25 StartAngle=2.44653 EndAngle=6.19048
    g4: ArcOfCircle CenterX=-11.5662 CenterY=-6.46424 CenterZ=0 NormalX=0 NormalY=0 NormalZ=1 AngleXU=0 Radius=10 StartAngle=5.58812 EndAngle=6.79283
    g5: Circle CenterX=-1.39 CenterY=-14.95 CenterZ=0 NormalX=0 NormalY=0 NormalZ=1 AngleXU=0 Radius=2.15
  constraints (14):
    c: Diameter(g0) = 3.4
    c: Coincident(g1,g0)
    c: Diameter(g1) = 6.5
    c: Coincident(g0,g-1)
    c: Distance(g3,g-1) = 14.95
    c: Diameter(g3) = 6.5
    c: Distance(g3,g-2) = 1.39
    c: Coincident(g5,g3)
    c: Diameter(g5) = 4.3
    c: Diameter(g4) = 20
    c: Tangent(g1,g4) = 1.5708
    c: Tangent(g1,g2) = 1.5708
    c: Tangent(g3,g2) = 1.5708
    c: Tangent(g3,g4) = 1.5708
FEATURE [PartDesign::Pad] Pad040
  Direction = (1,-2e-16,3e-16)
  Length = 3
  Length2 = 10
  Placement = pos=(0,0,0) rot=(0.57735,0.57735,0.57735;2.0944rad)
  Profile = -> Sketch091
  ReferenceAxis = -> Sketch091 [N_Axis]
  Type = 0
FEATURE [PartDesign::Body] Body015  label="Body008: Motor link A2 v0"
  Group = -> [Sketch091,Pad040]
  Origin = -> Origin015
  Placement = pos=(38,-16.2316,-10.6271) rot=(0,0.492424,0.870356;3.14159rad)
  Tip = -> Pad040
FEATURE [PartDesign::Pad] Pad041
  BaseFeature = -> Pad039
  Direction = (1,-1e-16,2e-16)
  Length = 3
  Length2 = 10
  Placement = pos=(0,0,0) rot=(1,0,0;1.5708rad)
  Profile = -> Sketch090
  ReferenceAxis = -> Sketch090 [N_Axis]
  Reversed = true
  Type = 0
FEATURE [PartDesign::Fillet] Fillet005
  Base = -> Pad041 [Edge29]
  BaseFeature = -> Pad041
  Placement = pos=(0,0,0) rot=(1,0,0;1.5708rad)
  Radius = 2
  SupportTransform = false
  UseAllEdges = false
FEATURE [Sketcher::SketchObject] Sketch092
  AttachmentOffset = pos=(0,0,20) rot=(0,0,1;0rad)
  FullyConstrained = true
  MapMode = 5
  Placement = pos=(20,-4.4e-15,4.4e-15) rot=(0.57735,0.57735,0.57735;2.0944rad)
  Support = -> [YZ_Plane014]
  sketch-geometry (3):
    g0: Circle CenterX=-14.8 CenterY=-27.7 CenterZ=0 NormalX=0 NormalY=0 NormalZ=1 AngleXU=0 Radius=13
    g1: LineSegment StartX=0 StartY=0 StartZ=0 EndX=-14.8 EndY=-27.7 EndZ=0
    g2: Circle CenterX=-19.2769 CenterY=-36.079 CenterZ=0 NormalX=0 NormalY=0 NormalZ=1 AngleXU=0 Radius=22.5
  constraints (8):
    c: Diameter(g0) = 26
    c: Distance(g0,g-2) = 14.8
    c: Distance(g0,g-1) = 27.7
    c: Coincident(g1,g-1)
    c: Coincident(g1,g0)
    c: PointOnObject(g2,g1)
    c: Tangent(g2,g0)
    c: Diameter(g2) = 45
FEATURE [PartDesign::Pocket] Pocket031
  BaseFeature = -> Fillet005
  Direction = (-1,2e-16,-3e-16)
  Length = 5
  Length2 = 5
  Placement = pos=(0,0,0) rot=(1,0,0;1.5708rad)
  Profile = -> Sketch092
  ReferenceAxis = -> Sketch092 [N_Axis]
  Reversed = true
  Type = 0
FEATURE [Sketcher::SketchObject] Sketch093
  FullyConstrained = true
  MapMode = 5
  Placement = pos=(0,-32,1.41e-14) rot=(1,0,0;1.5708rad)
  Support = -> [Pocket031]
  sketch-geometry (2):
    g0: Circle CenterX=0 CenterY=0 CenterZ=0 NormalX=0 NormalY=0 NormalZ=1 AngleXU=0 Radius=25.1
    g1: Circle CenterX=0 CenterY=0 CenterZ=0 NormalX=0 NormalY=0 NormalZ=1 AngleXU=0 Radius=22.4
  constraints (4):
    c: Coincident(g0,g-1)
    c: Diameter(g0) = 50.2
    c: Coincident(g1,g0)
    c: Diameter(g1) = 44.8
FEATURE [PartDesign::Pad] Pad042
  BaseFeature = -> Pocket031
  Direction = (0,-1,2e-16)
  Length = 20.5
  Length2 = 10
  Placement = pos=(0,0,0) rot=(1,0,0;1.5708rad)
  Profile = -> Sketch093
  ReferenceAxis = -> Sketch093 [N_Axis]
  Type = 0
FEATURE [Sketcher::SketchObject] Sketch094
  AttachmentOffset = pos=(0,0,8) rot=(0,0,1;0rad)
  FullyConstrained = true
  MapMode = 5
  Placement = pos=(0,24,-1.06e-14) rot=(-1,0,0;1.5708rad)
  Support = -> [Pad042]
  sketch-geometry (2):
    g0: Circle CenterX=0 CenterY=0 CenterZ=0 NormalX=0 NormalY=0 NormalZ=1 AngleXU=0 Radius=30
    g1: Circle CenterX=0 CenterY=0 CenterZ=0 NormalX=0 NormalY=0 NormalZ=1 AngleXU=0 Radius=22.4
  constraints (4):
    c: Coincident(g0,g-1)
    c: Coincident(g1,g0)
    c: Diameter(g1) = 44.8
    c: Diameter(g0) = 60
FEATURE [PartDesign::AdditiveLoft] AdditiveLoft001
  BaseFeature = -> Pad042
  Closed = false
  Placement = pos=(0,0,0) rot=(1,0,0;1.5708rad)
  Profile = -> Sketch094
  Ruled = false
  Sections = -> [Pad042]
FEATURE [Sketcher::SketchObject] Sketch095
  FullyConstrained = true
  MapMode = 5
  Placement = pos=(0,24,-1.22e-14) rot=(-1,0,0;1.5708rad)
  Support = -> [AdditiveLoft001]
  sketch-geometry (2):
    g0: Circle CenterX=0 CenterY=0 CenterZ=0 NormalX=0 NormalY=0 NormalZ=1 AngleXU=0 Radius=30
    g1: Circle CenterX=0 CenterY=0 CenterZ=0 NormalX=0 NormalY=0 NormalZ=1 AngleXU=0 Radius=25.2
  constraints (4):
    c: Coincident(g0,g-1)
    c: Coincident(g1,g0)
    c: Diameter(g1) = 50.4
    c: Diameter(g0) = 60
FEATURE [PartDesign::Pad] Pad043
  BaseFeature = -> AdditiveLoft001
  Direction = (0,1,-4e-16)
  Length = 20
  Length2 = 10
  Placement = pos=(0,0,0) rot=(1,0,0;1.5708rad)
  Profile = -> Sketch095
  ReferenceAxis = -> Sketch095 [N_Axis]
  Type = 0
FEATURE [PartDesign::Body] Body014  label="Body014: Housing v0"
  Group = -> [Sketch079,Pad036,Sketch080,Pad037,Sketch081,Pad038,Sketch082,Pocket024,Sketch083,Pocket025,Sketch084,Pocket026,Sketch085,Pocket027,Sketch086,Pocket028,Sketch087,Pocket029,Sketch088,Pocket030,Sketch089,Pad039,Sketch090,Pad041,Fillet005,Sketch092,Pocket031,Sketch093,Pad042,Sketch094,AdditiveLoft001,Sketch095,Pad043]
  Origin = -> Origin014
  Tip = -> Pad043
FEATURE [Sketcher::SketchObject] Sketch096
  FullyConstrained = true
  MapMode = 5
  Placement = pos=(0,0,0) rot=(0.57735,0.57735,0.57735;2.0944rad)
  Support = -> [YZ_Plane016]
  sketch-geometry (16):
    g0: Circle CenterX=0 CenterY=0 CenterZ=0 NormalX=0 NormalY=0 NormalZ=1 AngleXU=0 Radius=1.7
    g1: ArcOfCircle CenterX=0 CenterY=0 CenterZ=0 NormalX=0 NormalY=0 NormalZ=1 AngleXU=0 Radius=3.25 StartAngle=6.19048 EndAngle=7.85398
    g2: LineSegment StartX=3.23604 StartY=-0.300876 StartZ=0 EndX=1.84604 EndY=-15.2509 EndZ=0
    g3: ArcOfCircle CenterX=-1.39 CenterY=-14.95 CenterZ=0 NormalX=0 NormalY=0 NormalZ=1 AngleXU=0 Radius=3.25 StartAngle=2.44653 EndAngle=6.19048
    g4: ArcOfCircle CenterX=-11.5662 CenterY=-6.46424 CenterZ=0 NormalX=0 NormalY=0 NormalZ=1 AngleXU=0 Radius=10 StartAngle=5.58812 EndAngle=6.79283
    g5: Circle CenterX=-1.39 CenterY=-14.95 CenterZ=0 NormalX=0 NormalY=0 NormalZ=1 AngleXU=0 Radius=2.15
    g6: Circle CenterX=-16.2 CenterY=9.35 CenterZ=0 NormalX=0 NormalY=0 NormalZ=1 AngleXU=0 Radius=1.7
    g7: ArcOfCircle CenterX=-16.2 CenterY=9.35 CenterZ=0 NormalX=0 NormalY=0 NormalZ=1 AngleXU=0 Radius=3.25 StartAngle=4.74624 EndAngle=4.76194
    g8: ArcOfCircle CenterX=-15.7516 CenterY=-3.89241 CenterZ=0 NormalX=0 NormalY=0 NormalZ=1 AngleXU=0 Radius=10 StartAngle=1.60465 EndAngle=2.79969
    g9: ArcOfCircle CenterX=-28.2346 CenterY=0.55 CenterZ=0 NormalX=0 NormalY=0 NormalZ=1 AngleXU=0 Radius=3.25 StartAngle=2.20217 EndAngle=5.94129
    g10: Circle CenterX=-28.2346 CenterY=0.55 CenterZ=0 NormalX=0 NormalY=0 NormalZ=1 AngleXU=0 Radius=2.15
    g11: LineSegment StartX=-30.153 StartY=3.17345 StartZ=0 EndX=-18.1183 EndY=11.9735 EndZ=0
    g12: ArcOfCircle CenterX=0 CenterY=18.7092 CenterZ=0 NormalX=0 NormalY=0 NormalZ=1 AngleXU=0 Radius=15.4592 StartAngle=3.66548 EndAngle=4.71239
    g13: ArcOfCircle CenterX=-15.3456 CenterY=-7.87883 CenterZ=0 NormalX=0 NormalY=0 NormalZ=1 AngleXU=0 Radius=14 StartAngle=0.474331 EndAngle=1.62035
    g14: ArcOfCircle CenterX=-16.2 CenterY=9.35 CenterZ=0 NormalX=0 NormalY=0 NormalZ=1 AngleXU=0 Radius=3.25 StartAngle=0.523883 EndAngle=2.20217
    g15: ArcOfCircle CenterX=0 CenterY=0 CenterZ=0 NormalX=0 NormalY=0 NormalZ=1 AngleXU=0 Radius=3.25 StartAngle=3.61592 EndAngle=3.65124
  constraints (39):
    c: Diameter(g0) = 3.4
    c: Coincident(g1,g0)
    c: Diameter(g1) = 6.5
    c: Coincident(g0,g-1)
    c: Distance(g3,g-1) = 14.95
    c: Diameter(g3) = 6.5
    c: Distance(g3,g-2) = 1.39
    c: Coincident(g5,g3)
    c: Diameter(g5) = 4.3
    c: Diameter(g4) = 20
    c: Tangent(g1,g2) = 1.5708
    c: Tangent(g3,g2) = 1.5708
    c: Tangent(g3,g4) = 1.5708
    c: Coincident(g7,g6)
    c: Coincident(g10,g9)
    c: Tangent(g9,g8) = 1.5708
    c: Tangent(g8,g7) = 1.5708
    c: Equal(g1,g7)
    c: Equal(g6,g0)
    c: Equal(g10,g5)
    c: Equal(g9,g3)
    c: Distance(g9,g-1) = 0.55
    c: Distance(g9,g0) = 28.24
    c: Distance(g6,g-1) = 9.35
    c: Distance(g6,g-2) = 16.2
    c: Equal(g8,g4)
    c: Tangent(g9,g11) = 1.5708
    c: PointOnObject(g12,g-2)
    c: Diameter(g13) = 28
    c: Equal(g7,g14)
    c: Tangent(g7,g13) = 1.5708
    c: Tangent(g14,g12) = 1.5708
    c: Coincident(g7,g14)
    c: Equal(g1,g15)
    c: Tangent(g1,g12) = 1.5708
    c: Tangent(g15,g13) = 1.5708
    c: Coincident(g1,g15)
    c: Tangent(g15,g4) = 1.5708
    c: Tangent(g11,g14) = 1.5708
FEATURE [PartDesign::Pad] Pad044
  Direction = (1,-2e-16,3e-16)
  Length = 3
  Length2 = 10
  Placement = pos=(0,0,0) rot=(0.57735,0.57735,0.57735;2.0944rad)
  Profile = -> Sketch096
  ReferenceAxis = -> Sketch096 [N_Axis]
  Type = 0
FEATURE [PartDesign::Body] Body016  label="Body008: Motor link v001"
  Group = -> [Sketch096,Pad044]
  Origin = -> Origin016
  Placement = pos=(35,0,-20) rot=(0,0,1;0rad)
  Tip = -> Pad044
FEATURE [Part::Part2DObjectPython] InvoluteGear003  # Draft 2D object (typed FeaturePython)
  ExternalGear = true
  HighPrecision = true
  Modules = 1
  NumberOfTeeth = 10
  PressureAngle = 20
FEATURE [PartDesign::Pad] Pad045
  Direction = (0,0,1)
  Length = 8
  Length2 = 10
  Profile = -> InvoluteGear003
  ReferenceAxis = -> InvoluteGear003 [N_Axis]
  Type = 0
FEATURE [Sketcher::SketchObject] Sketch097
  FullyConstrained = true
  MapMode = 5
  Support = -> [XY_Plane017]
  sketch-geometry (4):
    g0: ArcOfCircle CenterX=0 CenterY=0 CenterZ=0 NormalX=0 NormalY=0 NormalZ=1 AngleXU=0 Radius=2.625 StartAngle=2.47406 EndAngle=3.80912
    g1: LineSegment StartX=-2.06155 StartY=1.625 StartZ=0 EndX=2.06155 EndY=1.625 EndZ=0
    g2: LineSegment StartX=-2.06155 StartY=-1.625 StartZ=0 EndX=2.06155 EndY=-1.625 EndZ=0
    g3: ArcOfCircle CenterX=0 CenterY=0 CenterZ=0 NormalX=0 NormalY=0 NormalZ=1 AngleXU=0 Radius=2.625 StartAngle=5.61566 EndAngle=6.95071
  constraints (12):
    c: Coincident(g0,g-1)
    c: Diameter(g0) = 5.25
    c: Horizontal(g1)
    c: Horizontal(g2)
    c: Equal(g1,g2)
    c: Distance(g1,g2) = 3.25
    c: Coincident(g3,g1)
    c: Coincident(g0,g1)
    c: Equal(g0,g3)
    c: Coincident(g0,g2)
    c: Coincident(g3,g2)
    c: Coincident(g0,g3)
FEATURE [PartDesign::Pocket] Pocket032
  BaseFeature = -> Pad045
  Direction = (0,0,-1)
  Length = 5
  Length2 = 5
  Profile = -> Sketch097
  ReferenceAxis = -> Sketch097 [N_Axis]
  Reversed = true
  Type = 1
FEATURE [PartDesign::Body] Body017  label="Body008: Pinion v001"
  Group = -> [InvoluteGear003,Pad045,Sketch097,Pocket032]
  Origin = -> Origin017
  Placement = pos=(41.6153,-11.97,-21.5) rot=(0,1,0;1.5708rad)
  Tip = -> Pocket032
FEATURE [Part::Part2DObjectPython] InvoluteGear004  # Draft 2D object (typed FeaturePython)
  ExternalGear = true
  HighPrecision = true
  Modules = 1
  NumberOfTeeth = 10
  PressureAngle = 20
FEATURE [PartDesign::Pad] Pad046
  Direction = (0,0,1)
  Length = 8
  Length2 = 10
  Profile = -> InvoluteGear004
  ReferenceAxis = -> InvoluteGear004 [N_Axis]
  Type = 0
FEATURE [Sketcher::SketchObject] Sketch098
  FullyConstrained = true
  MapMode = 5
  Support = -> [XY_Plane018]
  sketch-geometry (4):
    g0: ArcOfCircle CenterX=0 CenterY=0 CenterZ=0 NormalX=0 NormalY=0 NormalZ=1 AngleXU=0 Radius=2.575 StartAngle=2.48345 EndAngle=3.79974
    g1: LineSegment StartX=-2.03715 StartY=1.575 StartZ=0 EndX=2.03715 EndY=1.575 EndZ=0
    g2: LineSegment StartX=-2.03715 StartY=-1.575 StartZ=0 EndX=2.03715 EndY=-1.575 EndZ=0
    g3: ArcOfCircle CenterX=0 CenterY=0 CenterZ=0 NormalX=0 NormalY=0 NormalZ=1 AngleXU=0 Radius=2.575 StartAngle=5.62504 EndAngle=6.94133
  constraints (12):
    c: Coincident(g0,g-1)
    c: Diameter(g0) = 5.15
    c: Horizontal(g1)
    c: Horizontal(g2)
    c: Equal(g1,g2)
    c: Distance(g1,g2) = 3.15
    c: Coincident(g3,g1)
    c: Coincident(g0,g1)
    c: Equal(g0,g3)
    c: Coincident(g0,g2)
    c: Coincident(g3,g2)
    c: Coincident(g0,g3)
FEATURE [PartDesign::Pocket] Pocket033
  BaseFeature = -> Pad046
  Direction = (0,0,-1)
  Length = 5
  Length2 = 5
  Profile = -> Sketch098
  ReferenceAxis = -> Sketch098 [N_Axis]
  Reversed = true
  Type = 1
FEATURE [PartDesign::Body] Body018  label="Body008: Pinion v002"
  Group = -> [InvoluteGear004,Pad046,Sketch098,Pocket033]
  Origin = -> Origin018
  Placement = pos=(41.6153,-11.97,-21.5) rot=(0,1,0;1.5708rad)
  Tip = -> Pocket033
